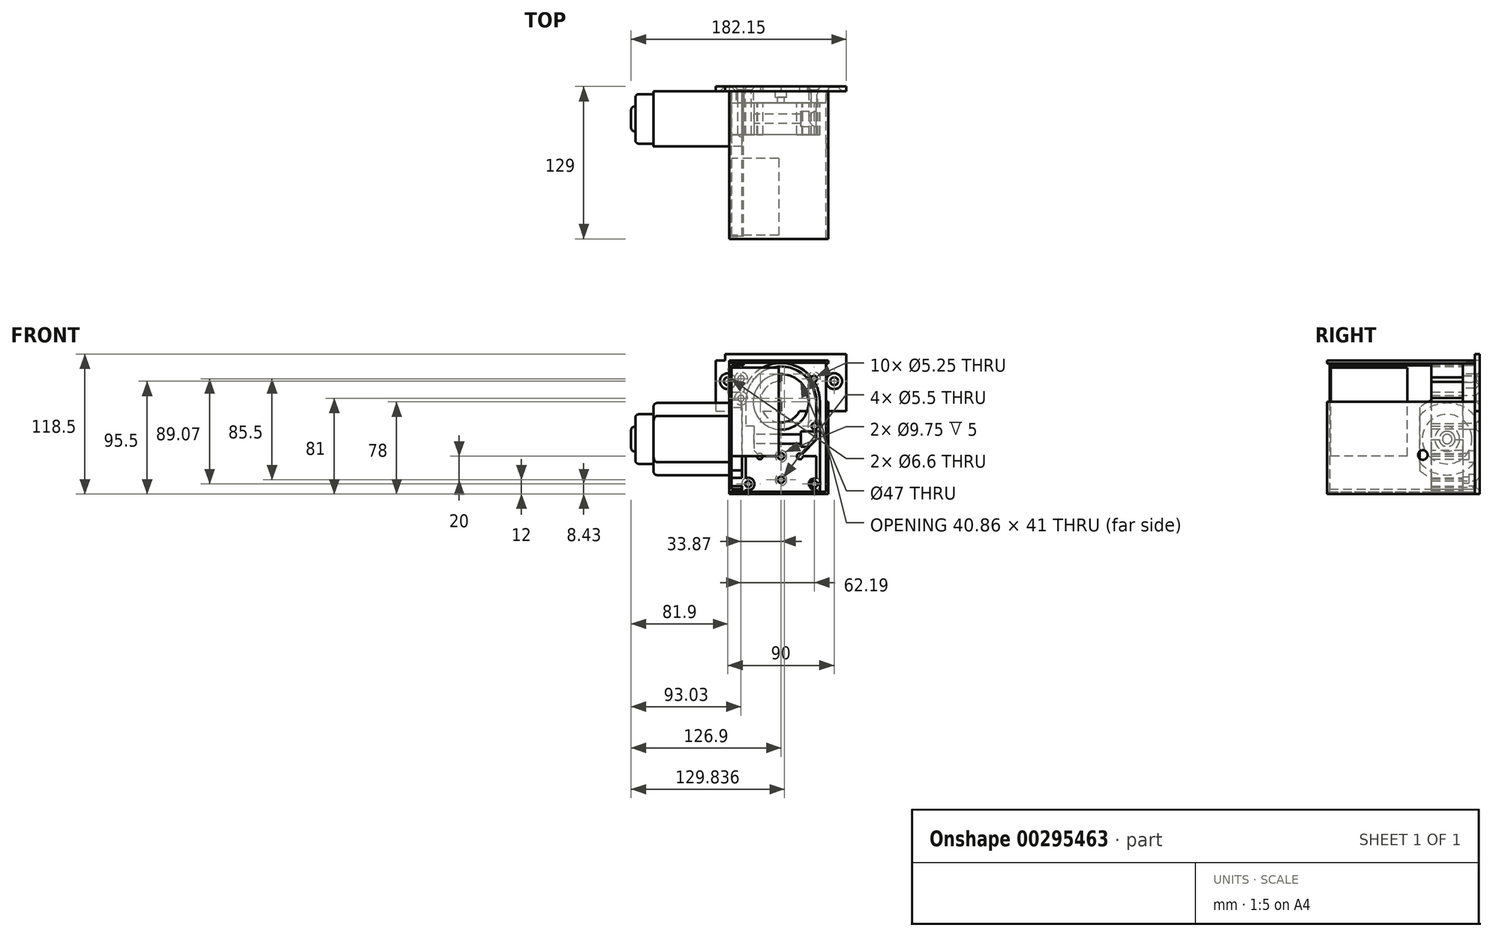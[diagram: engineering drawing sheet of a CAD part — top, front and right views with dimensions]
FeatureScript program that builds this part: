
annotation { "Feature Type Name" : "Feature", "Feature Type Description" : "" }
export const myFeature = defineFeature(function(context is Context, id is Id, definition is map)
    precondition{}
    {
        {
            var Q0;
            Q0=qCreatedBy(makeId("Front.planeOp"),FACE);
            cPlane(context, id + "F0", {"entities" : qUnion([Q0]), "cplaneType" : CPlaneType.OFFSET, "offset" : 4 * mm, "width" : 150 * mm, "height" : 150 * mm});
        }
        {
            var Q0;
            Q0=qCreatedBy(makeId("Front.planeOp"),FACE);
            cPlane(context, id + "F1", {"entities" : qUnion([Q0]), "cplaneType" : CPlaneType.OFFSET, "offset" : 14 * mm, "width" : 150 * mm, "height" : 150 * mm});
        }
        {
            var Q0;
            Q0=qCreatedBy(id+"F1.planeOp",FACE);
            var sketch = newSketch(context, id + "F2", { "sketchPlane" : qUnion([Q0])});
            skLineSegment(sketch, "E0", {"start": v(-56.01, 0) * mm, "end": v(61.33, 0) * mm, "construction": true});
            skLineSegment(sketch, "E1", {"start": v(0, 42.96) * mm, "end": v(0, -44.48) * mm, "construction": true});
            skLineSegment(sketch, "E2", {"start": v(55.25, 0) * mm, "end": v(55.25, 35) * mm});
            skLineSegment(sketch, "E3", {"start": v(55.25, 35) * mm, "end": v(0, 35) * mm});
            skLineSegment(sketch, "E4", {"start": v(0, 35) * mm, "end": v(-55.25, 35) * mm});
            skLineSegment(sketch, "E5", {"start": v(-55.25, 35) * mm, "end": v(-55.25, -35) * mm});
            skLineSegment(sketch, "E6", {"start": v(-55.25, -35) * mm, "end": v(55.25, -35) * mm});
            skLineSegment(sketch, "E7", {"start": v(55.25, -35) * mm, "end": v(55.25, 0) * mm});
            skLineSegment(sketch, "E8", {"start": v(-45, 0) * mm, "end": v(-45, 17.5) * mm, "construction": true});
            skLineSegment(sketch, "E9", {"start": v(-45, 17.5) * mm, "end": v(0, 17.5) * mm, "construction": true});
            skPoint(sketch, "E10", {"position": v(-45, 17.5) * mm});
            skPoint(sketch, "E11.MirrorP", {"position": v(45, 17.5) * mm});
            skCircle(sketch, "E12", {"center": v(0, 0) * mm, "radius": 23.5 * mm});
            skLineSegment(sketch, "E13.0", {"start": v(-53.25, 33) * mm, "end": v(-53.25, -35) * mm});
            skLineSegment(sketch, "E13.1", {"start": v(53.25, -35) * mm, "end": v(53.25, 0) * mm});
            skLineSegment(sketch, "E13.2", {"start": v(53.25, 0) * mm, "end": v(53.25, 33) * mm});
            skLineSegment(sketch, "E13.3", {"start": v(53.25, 33) * mm, "end": v(0, 33) * mm});
            skLineSegment(sketch, "E13.4", {"start": v(0, 33) * mm, "end": v(-53.25, 33) * mm});
            skCircle(sketch, "E14", {"center": v(0, 0) * mm, "radius": 32.9 * mm});
            skPoint(sketch, "E15", {"position": v(-32.9, 0) * mm});
            skLineSegment(sketch, "E16", {"start": v(-32.9, 0) * mm, "end": v(-32.9, -35) * mm});
            skLineSegment(sketch, "E17", {"start": v(-32.9, 0) * mm, "end": v(-55.25, 0) * mm});
            skLineSegment(sketch, "E18", {"start": v(-32.9, 0) * mm, "end": v(-32.9, 33) * mm});
            skLineSegment(sketch, "E19", {"start": v(-32.9, -35) * mm, "end": v(-32.9, -76) * mm});
            skLineSegment(sketch, "E20", {"start": v(-32.9, -76) * mm, "end": v(32.9, -76) * mm});
            skLineSegment(sketch, "E21", {"start": v(32.9, -76) * mm, "end": v(32.9, 33) * mm});
            skLineSegment(sketch, "E22", {"start": v(-41.9, 33) * mm, "end": v(-41.9, -76) * mm});
            skLineSegment(sketch, "E23", {"start": v(-41.9, -76) * mm, "end": v(-32.9, -76) * mm});
            skLineSegment(sketch, "E24", {"start": v(38.1, -76) * mm, "end": v(32.9, -76) * mm});
            skLineSegment(sketch, "E25", {"start": v(38.1, -76) * mm, "end": v(38.1, 33) * mm});
            skCircle(sketch, "E26", {"center": v(-45, 17.5) * mm, "radius": 6.75 * mm});
            skSolve(sketch);
        }
        {
            var Q0;
            Q0=qCreatedBy(id+"F0.planeOp",FACE);
            var sketch = newSketch(context, id + "F3", { "sketchPlane" : qUnion([Q0])});
            skCircle(sketch, "E27.0", {"center": v(0, 0) * mm, "radius": 23.5 * mm});
            skCircle(sketch, "E28.0", {"center": v(0, 0) * mm, "radius": 32.9 * mm, "construction": true});
            skLineSegment(sketch, "E29.0", {"start": v(53.25, 33) * mm, "end": v(0, 33) * mm});
            skLineSegment(sketch, "E29.1", {"start": v(0, 33) * mm, "end": v(-53.25, 33) * mm});
            skLineSegment(sketch, "E29.2", {"start": v(-53.25, 33) * mm, "end": v(-53.25, -35) * mm});
            skLineSegment(sketch, "E29.3", {"start": v(53.25, 0) * mm, "end": v(53.25, 33) * mm});
            skLineSegment(sketch, "E29.4", {"start": v(53.25, -35) * mm, "end": v(53.25, 0) * mm});
            skLineSegment(sketch, "E29.5", {"start": v(55.25, -35) * mm, "end": v(55.25, 0) * mm});
            skLineSegment(sketch, "E29.6", {"start": v(55.25, 0) * mm, "end": v(55.25, 35) * mm});
            skLineSegment(sketch, "E29.7", {"start": v(55.25, 35) * mm, "end": v(0, 35) * mm});
            skLineSegment(sketch, "E29.8", {"start": v(0, 35) * mm, "end": v(-55.25, 35) * mm});
            skLineSegment(sketch, "E29.9", {"start": v(-55.25, 35) * mm, "end": v(-55.25, -35) * mm});
            skPoint(sketch, "E29.10", {"position": v(-45, 17.5) * mm});
            skPoint(sketch, "E29.11", {"position": v(45, 17.5) * mm});
            skLineSegment(sketch, "E29.12", {"start": v(-45, 17.5) * mm, "end": v(0, 17.5) * mm});
            skLineSegment(sketch, "E29.13", {"start": v(-45, 0) * mm, "end": v(-45, 17.5) * mm});
            skLineSegment(sketch, "E29.14", {"start": v(-56.01, 0) * mm, "end": v(61.33, 0) * mm});
            skLineSegment(sketch, "E29.15", {"start": v(0, 42.96) * mm, "end": v(0, -44.48) * mm});
            skLineSegment(sketch, "E29.18", {"start": v(-32.9, 0) * mm, "end": v(-32.9, -35) * mm, "construction": true});
            skLineSegment(sketch, "E30.0", {"start": v(-55.25, -35) * mm, "end": v(55.25, -35) * mm});
            skCircle(sketch, "E31", {"center": v(0, 0) * mm, "radius": 17.5 * mm});
            skLineSegment(sketch, "E32", {"start": v(-55.25, -8) * mm, "end": v(55.25, -8) * mm});
            skLineSegment(sketch, "E33", {"start": v(48.1, 35) * mm, "end": v(48.1, -8) * mm, "construction": true});
            skLineSegment(sketch, "E34.0", {"start": v(32.9, -76) * mm, "end": v(32.9, 33) * mm});
            skLineSegment(sketch, "E34.1", {"start": v(-32.9, -76) * mm, "end": v(32.9, -76) * mm});
            skLineSegment(sketch, "E34.2", {"start": v(-41.9, 33) * mm, "end": v(-41.9, -76) * mm});
            skLineSegment(sketch, "E34.3", {"start": v(-41.9, -76) * mm, "end": v(-32.9, -76) * mm});
            skLineSegment(sketch, "E35.0", {"start": v(38.1, -76) * mm, "end": v(38.1, 33) * mm});
            skLineSegment(sketch, "E35.1", {"start": v(38.1, -76) * mm, "end": v(32.9, -76) * mm});
            skLineSegment(sketch, "E36.0", {"start": v(40.1, -76) * mm, "end": v(40.1, -8) * mm});
            skLineSegment(sketch, "E37", {"start": v(38.1, -76) * mm, "end": v(40.1, -76) * mm});
            skLineSegment(sketch, "E38", {"start": v(-43.9, -35) * mm, "end": v(-43.9, -76) * mm});
            skLineSegment(sketch, "E39", {"start": v(-43.9, -76) * mm, "end": v(-41.9, -76) * mm});
            skLineSegment(sketch, "E40", {"start": v(-43.9, -76) * mm, "end": v(-43.9, -78) * mm});
            skLineSegment(sketch, "E41", {"start": v(-43.9, -78) * mm, "end": v(40.1, -78) * mm});
            skLineSegment(sketch, "E42", {"start": v(40.1, -78) * mm, "end": v(40.1, -76) * mm});
            skLineSegment(sketch, "E43", {"start": v(-43.9, -35) * mm, "end": v(-43.9, -8) * mm});
            skLineSegment(sketch, "E44", {"start": v(-55.25, 35) * mm, "end": v(-55.25, 40.5) * mm});
            skLineSegment(sketch, "E45", {"start": v(-55.25, 40.5) * mm, "end": v(55.25, 40.5) * mm});
            skLineSegment(sketch, "E46", {"start": v(55.25, 40.5) * mm, "end": v(55.25, 35) * mm});
            skLineSegment(sketch, "E47.bottom", {"start": v(-55.25, 40.5) * mm, "end": v(-47.25, 40.5) * mm});
            skLineSegment(sketch, "E47.top", {"start": v(-55.25, 32.5) * mm, "end": v(-47.25, 32.5) * mm});
            skLineSegment(sketch, "E47.left", {"start": v(-55.25, 40.5) * mm, "end": v(-55.25, 32.5) * mm});
            skLineSegment(sketch, "E47.right", {"start": v(-47.25, 40.5) * mm, "end": v(-47.25, 32.5) * mm});
            skLineSegment(sketch, "E48.bottom", {"start": v(-47.25, 32.5) * mm, "end": v(47.25, 32.5) * mm});
            skLineSegment(sketch, "E48.top", {"start": v(-47.25, 0.5) * mm, "end": v(47.25, 0.5) * mm});
            skLineSegment(sketch, "E48.left", {"start": v(-47.25, 32.5) * mm, "end": v(-47.25, 0.5) * mm});
            skLineSegment(sketch, "E48.right", {"start": v(47.25, 32.5) * mm, "end": v(47.25, 0.5) * mm});
            skSolve(sketch);
        }
        {
            var Q0;
            {var subQ5=sQuery(id+"F3.wireOp",EDGE,"E48.left");Q0=makeQuery(id+"F3.imprint","IMPRINT",FACE,{"disambiguationData":[TD([[makeQuery(id+"F3.imprint","IMPRINT",EDGE,{"derivedFrom":subQ5}),-1.0]])]});}
            var Q1;
            {var subQ0=sQuery(id+"F3.wireOp",EDGE,"E32");var subQ1=makeQuery(id+"F3.imprint","INTERSECT",VERTEX,{"derivedFrom":[subQ0,sQuery(id+"F3.wireOp",EDGE,"E36.0")]});Q1=makeQuery(id+"F3.imprint","IMPRINT",FACE,{"disambiguationData":[TD([[makeQuery(id+"F3.imprint","IMPRINT",EDGE,{"disambiguationData":[TD([[subQ1,1.0]])],"derivedFrom":subQ0}),1.0]])]});}
            var Q2;
            {var subQ0=sQuery(id+"F3.wireOp",EDGE,"E29.13");var subQ1=sQuery(id+"F3.wireOp",EDGE,"E29.12");var subQ2=makeQuery(id+"F3.imprint","INTERSECT",VERTEX,{"derivedFrom":[subQ1,subQ0]});Q2=makeQuery(id+"F3.imprint","IMPRINT",FACE,{"disambiguationData":[TD([[makeQuery(id+"F3.imprint","IMPRINT",EDGE,{"disambiguationData":[TD([[subQ2,-1.0]])],"derivedFrom":subQ1}),-1.0]])]});}
            var Q3;
            {var subQ0=sQuery(id+"F3.wireOp",EDGE,"E29.14");var subQ1=sQuery(id+"F3.wireOp",EDGE,"E29.13");var subQ2=makeQuery(id+"F3.imprint","INTERSECT",VERTEX,{"derivedFrom":[subQ1,subQ0]});Q3=makeQuery(id+"F3.imprint","IMPRINT",FACE,{"disambiguationData":[TD([[makeQuery(id+"F3.imprint","IMPRINT",EDGE,{"disambiguationData":[TD([[subQ2,-1.0]])],"derivedFrom":subQ1}),-1.0]])]});}
            var Q4;
            {var subQ5=sQuery(id+"F3.wireOp",EDGE,"E29.3");Q4=makeQuery(id+"F3.imprint","IMPRINT",FACE,{"disambiguationData":[TD([[makeQuery(id+"F3.imprint","IMPRINT",EDGE,{"derivedFrom":subQ5}),1.0]])]});}
            var Q5;
            {var subQ5=sQuery(id+"F3.wireOp",EDGE,"E29.3");Q5=makeQuery(id+"F3.imprint","IMPRINT",FACE,{"disambiguationData":[TD([[makeQuery(id+"F3.imprint","IMPRINT",EDGE,{"derivedFrom":subQ5}),-1.0]])]});}
            var Q6;
            {var subQ1=sQuery(id+"F3.wireOp",EDGE,"E29.12");var subQ5=sQuery(id+"F3.wireOp",EDGE,"E34.2");var subQ6=makeQuery(id+"F3.imprint","INTERSECT",VERTEX,{"derivedFrom":[subQ1,subQ5]});Q6=makeQuery(id+"F3.imprint","IMPRINT",FACE,{"disambiguationData":[TD([[makeQuery(id+"F3.imprint","IMPRINT",EDGE,{"disambiguationData":[TD([[subQ6,-1.0]])],"derivedFrom":subQ1}),1.0]])]});}
            var Q7;
            {var subQ3=sQuery(id+"F3.wireOp",EDGE,"E32");var subQ5=sQuery(id+"F3.wireOp",EDGE,"E29.5");var subQ7=makeQuery(id+"F3.imprint","INTERSECT",VERTEX,{"derivedFrom":[subQ5,subQ3]});Q7=makeQuery(id+"F3.imprint","IMPRINT",FACE,{"disambiguationData":[TD([[makeQuery(id+"F3.imprint","IMPRINT",EDGE,{"disambiguationData":[TD([[subQ7,1.0]])],"derivedFrom":subQ3}),1.0]])]});}
            var Q8;
            {var subQ1=sQuery(id+"F3.wireOp",EDGE,"E29.1");var subQ7=makeQuery(id+"F3.imprint","INTERSECT",VERTEX,{"derivedFrom":[subQ1,sQuery(id+"F3.wireOp",EDGE,"E34.2")]});Q8=makeQuery(id+"F3.imprint","IMPRINT",FACE,{"disambiguationData":[TD([[makeQuery(id+"F3.imprint","IMPRINT",EDGE,{"disambiguationData":[TD([[subQ7,-1.0]])],"derivedFrom":subQ1}),-1.0]])]});}
            var Q9;
            {var subQ0=sQuery(id+"F3.wireOp",EDGE,"E31");var subQ1=sQuery(id+"F3.wireOp",EDGE,"E29.14");var subQ2=makeQuery(id+"F3.imprint","INTERSECT",VERTEX,{"disambiguationData":[OD(1.0)],"derivedFrom":[subQ1,subQ0]});Q9=makeQuery(id+"F3.imprint","IMPRINT",FACE,{"disambiguationData":[TD([[makeQuery(id+"F3.imprint","IMPRINT",EDGE,{"disambiguationData":[TD([[subQ2,-1.0]])],"derivedFrom":subQ1}),1.0]])]});}
            var Q10;
            {var subQ1=sQuery(id+"F3.wireOp",EDGE,"E29.12");var subQ3=sQuery(id+"F3.wireOp",EDGE,"E27.0");var subQ4=makeQuery(id+"F3.imprint","INTERSECT",VERTEX,{"derivedFrom":[subQ1,subQ3]});Q10=makeQuery(id+"F3.imprint","IMPRINT",FACE,{"disambiguationData":[TD([[makeQuery(id+"F3.imprint","IMPRINT",EDGE,{"disambiguationData":[TD([[subQ4,1.0]])],"derivedFrom":subQ3}),1.0]])]});}
            var Q11;
            {var subQ1=sQuery(id+"F3.wireOp",EDGE,"E29.12");var subQ3=sQuery(id+"F3.wireOp",EDGE,"E27.0");var subQ4=makeQuery(id+"F3.imprint","INTERSECT",VERTEX,{"derivedFrom":[subQ1,subQ3]});Q11=makeQuery(id+"F3.imprint","IMPRINT",FACE,{"disambiguationData":[TD([[makeQuery(id+"F3.imprint","IMPRINT",EDGE,{"disambiguationData":[TD([[subQ4,-1.0]])],"derivedFrom":subQ3}),1.0]])]});}
            var Q12;
            {var subQ0=sQuery(id+"F3.wireOp",EDGE,"E27.0");var subQ1=sQuery(id+"F3.wireOp",EDGE,"E29.14");var subQ2=makeQuery(id+"F3.imprint","INTERSECT",VERTEX,{"disambiguationData":[OD(0.0)],"derivedFrom":[subQ1,subQ0]});Q12=makeQuery(id+"F3.imprint","IMPRINT",FACE,{"disambiguationData":[TD([[makeQuery(id+"F3.imprint","IMPRINT",EDGE,{"disambiguationData":[TD([[subQ2,-1.0]])],"derivedFrom":subQ1}),-1.0]])]});}
            var Q13;
            {var subQ0=sQuery(id+"F3.wireOp",EDGE,"E31");var subQ1=sQuery(id+"F3.wireOp",EDGE,"E29.14");var subQ2=makeQuery(id+"F3.imprint","INTERSECT",VERTEX,{"disambiguationData":[OD(1.0)],"derivedFrom":[subQ1,subQ0]});Q13=makeQuery(id+"F3.imprint","IMPRINT",FACE,{"disambiguationData":[TD([[makeQuery(id+"F3.imprint","IMPRINT",EDGE,{"disambiguationData":[TD([[subQ2,-1.0]])],"derivedFrom":subQ1}),-1.0]])]});}
            var Q14;
            {var subQ0=sQuery(id+"F3.wireOp",EDGE,"E30.0");var subQ1=sQuery(id+"F3.wireOp",EDGE,"E29.15");var subQ2=makeQuery(id+"F3.imprint","INTERSECT",VERTEX,{"derivedFrom":[subQ1,subQ0]});Q14=makeQuery(id+"F3.imprint","IMPRINT",FACE,{"disambiguationData":[TD([[makeQuery(id+"F3.imprint","IMPRINT",EDGE,{"disambiguationData":[TD([[subQ2,1.0]])],"derivedFrom":subQ1}),1.0]])]});}
            var Q15;
            {var subQ0=sQuery(id+"F3.wireOp",EDGE,"E30.0");var subQ1=sQuery(id+"F3.wireOp",EDGE,"E29.15");var subQ2=makeQuery(id+"F3.imprint","INTERSECT",VERTEX,{"derivedFrom":[subQ1,subQ0]});Q15=makeQuery(id+"F3.imprint","IMPRINT",FACE,{"disambiguationData":[TD([[makeQuery(id+"F3.imprint","IMPRINT",EDGE,{"disambiguationData":[TD([[subQ2,1.0]])],"derivedFrom":subQ1}),-1.0]])]});}
            var Q16;
            {var subQ0=sQuery(id+"F3.wireOp",EDGE,"E31");var subQ1=sQuery(id+"F3.wireOp",EDGE,"E29.15");var subQ2=makeQuery(id+"F3.imprint","INTERSECT",VERTEX,{"derivedFrom":[subQ1,subQ0]});Q16=makeQuery(id+"F3.imprint","IMPRINT",FACE,{"disambiguationData":[TD([[makeQuery(id+"F3.imprint","IMPRINT",EDGE,{"disambiguationData":[TD([[subQ2,-1.0]])],"derivedFrom":subQ1}),-1.0]])]});}
            var Q17;
            {var subQ0=sQuery(id+"F3.wireOp",EDGE,"E31");var subQ1=sQuery(id+"F3.wireOp",EDGE,"E29.15");var subQ2=makeQuery(id+"F3.imprint","INTERSECT",VERTEX,{"derivedFrom":[subQ1,subQ0]});Q17=makeQuery(id+"F3.imprint","IMPRINT",FACE,{"disambiguationData":[TD([[makeQuery(id+"F3.imprint","IMPRINT",EDGE,{"disambiguationData":[TD([[subQ2,-1.0]])],"derivedFrom":subQ1}),1.0]])]});}
            var Q18;
            {var subQ0=sQuery(id+"F3.wireOp",EDGE,"E27.0");var subQ1=sQuery(id+"F3.wireOp",EDGE,"E29.14");var subQ2=makeQuery(id+"F3.imprint","INTERSECT",VERTEX,{"disambiguationData":[OD(1.0)],"derivedFrom":[subQ1,subQ0]});Q18=makeQuery(id+"F3.imprint","IMPRINT",FACE,{"disambiguationData":[TD([[makeQuery(id+"F3.imprint","IMPRINT",EDGE,{"disambiguationData":[TD([[subQ2,-1.0]])],"derivedFrom":subQ1}),-1.0]])]});}
            var Q19;
            {var subQ0=sQuery(id+"F3.wireOp",EDGE,"E34.2");var subQ1=sQuery(id+"F3.wireOp",EDGE,"E29.14");var subQ2=makeQuery(id+"F3.imprint","INTERSECT",VERTEX,{"derivedFrom":[subQ1,subQ0]});Q19=makeQuery(id+"F3.imprint","IMPRINT",FACE,{"disambiguationData":[TD([[makeQuery(id+"F3.imprint","IMPRINT",EDGE,{"disambiguationData":[TD([[subQ2,-1.0]])],"derivedFrom":subQ1}),-1.0]])]});}
            var Q20;
            {var subQ0=sQuery(id+"F3.wireOp",EDGE,"E34.2");var subQ1=sQuery(id+"F3.wireOp",EDGE,"E29.12");var subQ2=makeQuery(id+"F3.imprint","INTERSECT",VERTEX,{"derivedFrom":[subQ1,subQ0]});Q20=makeQuery(id+"F3.imprint","IMPRINT",FACE,{"disambiguationData":[TD([[makeQuery(id+"F3.imprint","IMPRINT",EDGE,{"disambiguationData":[TD([[subQ2,-1.0]])],"derivedFrom":subQ1}),-1.0]])]});}
            var Q21;
            {var subQ2=sQuery(id+"F3.wireOp",EDGE,"E29.2");var subQ4=sQuery(id+"F3.wireOp",EDGE,"E29.14");var subQ8=makeQuery(id+"F3.imprint","INTERSECT",VERTEX,{"derivedFrom":[subQ2,subQ4]});Q21=makeQuery(id+"F3.imprint","IMPRINT",FACE,{"disambiguationData":[TD([[makeQuery(id+"F3.imprint","IMPRINT",EDGE,{"disambiguationData":[TD([[subQ8,-1.0]])],"derivedFrom":subQ2}),1.0]])]});}
            var Q22;
            {var subQ0=sQuery(id+"F3.wireOp",EDGE,"E29.14");var subQ1=sQuery(id+"F3.wireOp",EDGE,"E29.2");var subQ2=makeQuery(id+"F3.imprint","INTERSECT",VERTEX,{"derivedFrom":[subQ1,subQ0]});Q22=makeQuery(id+"F3.imprint","IMPRINT",FACE,{"disambiguationData":[TD([[makeQuery(id+"F3.imprint","IMPRINT",EDGE,{"disambiguationData":[TD([[subQ2,-1.0]])],"derivedFrom":subQ1}),-1.0]])]});}
            var Q23;
            {var subQ0=sQuery(id+"F3.wireOp",EDGE,"E34.1");Q23=makeQuery(id+"F3.imprint","IMPRINT",FACE,{"disambiguationData":[TD([[makeQuery(id+"F3.imprint","IMPRINT",EDGE,{"derivedFrom":subQ0}),1.0]])]});}
            var Q24;
            {var subQ0=sQuery(id+"F3.wireOp",EDGE,"E27.0");var subQ1=sQuery(id+"F3.wireOp",EDGE,"E29.14");var subQ2=makeQuery(id+"F3.imprint","INTERSECT",VERTEX,{"disambiguationData":[OD(1.0)],"derivedFrom":[subQ1,subQ0]});Q24=makeQuery(id+"F3.imprint","IMPRINT",FACE,{"disambiguationData":[TD([[makeQuery(id+"F3.imprint","IMPRINT",EDGE,{"disambiguationData":[TD([[subQ2,-1.0]])],"derivedFrom":subQ1}),1.0]])]});}
            var Q25;
            {var subQ5=sQuery(id+"F3.wireOp",EDGE,"E35.1");Q25=makeQuery(id+"F3.imprint","IMPRINT",FACE,{"disambiguationData":[TD([[makeQuery(id+"F3.imprint","IMPRINT",EDGE,{"derivedFrom":subQ5}),-1.0]])]});}
            var Q26;
            {var subQ0=sQuery(id+"F3.wireOp",EDGE,"E34.0");var subQ1=sQuery(id+"F3.wireOp",EDGE,"E30.0");var subQ2=makeQuery(id+"F3.imprint","INTERSECT",VERTEX,{"derivedFrom":[subQ1,subQ0]});Q26=makeQuery(id+"F3.imprint","IMPRINT",FACE,{"disambiguationData":[TD([[makeQuery(id+"F3.imprint","IMPRINT",EDGE,{"disambiguationData":[TD([[subQ2,-1.0]])],"derivedFrom":subQ1}),1.0]])]});}
            var Q27;
            {var subQ0=sQuery(id+"F3.wireOp",EDGE,"E34.0");var subQ1=sQuery(id+"F3.wireOp",EDGE,"E29.14");var subQ2=makeQuery(id+"F3.imprint","INTERSECT",VERTEX,{"derivedFrom":[subQ1,subQ0]});Q27=makeQuery(id+"F3.imprint","IMPRINT",FACE,{"disambiguationData":[TD([[makeQuery(id+"F3.imprint","IMPRINT",EDGE,{"disambiguationData":[TD([[subQ2,-1.0]])],"derivedFrom":subQ1}),-1.0]])]});}
            var Q28;
            {var subQ0=sQuery(id+"F3.wireOp",EDGE,"E34.0");var subQ1=sQuery(id+"F3.wireOp",EDGE,"E29.0");var subQ2=makeQuery(id+"F3.imprint","INTERSECT",VERTEX,{"derivedFrom":[subQ1,subQ0]});Q28=makeQuery(id+"F3.imprint","IMPRINT",FACE,{"disambiguationData":[TD([[makeQuery(id+"F3.imprint","IMPRINT",EDGE,{"disambiguationData":[TD([[subQ2,1.0]])],"derivedFrom":subQ1}),1.0]])]});}
            var Q29;
            {var subQ5=sQuery(id+"F3.wireOp",EDGE,"E37");Q29=makeQuery(id+"F3.imprint","IMPRINT",FACE,{"disambiguationData":[TD([[makeQuery(id+"F3.imprint","IMPRINT",EDGE,{"derivedFrom":subQ5}),1.0]])]});}
            var Q30;
            {var subQ0=sQuery(id+"F3.wireOp",EDGE,"E36.0");var subQ1=sQuery(id+"F3.wireOp",EDGE,"E30.0");var subQ2=makeQuery(id+"F3.imprint","INTERSECT",VERTEX,{"derivedFrom":[subQ1,subQ0]});Q30=makeQuery(id+"F3.imprint","IMPRINT",FACE,{"disambiguationData":[TD([[makeQuery(id+"F3.imprint","IMPRINT",EDGE,{"disambiguationData":[TD([[subQ2,1.0]])],"derivedFrom":subQ1}),1.0]])]});}
            var Q31;
            {var subQ0=sQuery(id+"F3.wireOp",EDGE,"E38");Q31=makeQuery(id+"F3.imprint","IMPRINT",FACE,{"disambiguationData":[TD([[makeQuery(id+"F3.imprint","IMPRINT",EDGE,{"derivedFrom":subQ0}),1.0]])]});}
            var Q32;
            Q32=makeQuery(id+"F3.imprint","IMPRINT",FACE,{"disambiguationData":[TD([[makeQuery(id+"F3.imprint","IMPRINT",EDGE,{"derivedFrom":sQuery(id+"F3.wireOp",EDGE,"E34.1")}),-1.0]])]});
            var Q33;
            {var subQ0=sQuery(id+"F3.wireOp",EDGE,"E43");Q33=makeQuery(id+"F3.imprint","IMPRINT",FACE,{"disambiguationData":[TD([[makeQuery(id+"F3.imprint","IMPRINT",EDGE,{"derivedFrom":subQ0}),-1.0]])]});}
            var Q34;
            {var subQ5=sQuery(id+"F3.wireOp",EDGE,"E47.bottom");Q34=makeQuery(id+"F3.imprint","IMPRINT",FACE,{"disambiguationData":[TD([[makeQuery(id+"F3.imprint","IMPRINT",EDGE,{"derivedFrom":subQ5}),-1.0]])]});}
            var Q35;
            {var subQ1=sQuery(id+"F3.wireOp",EDGE,"E29.8");var subQ3=sQuery(id+"F3.wireOp",EDGE,"E47.right");var subQ4=makeQuery(id+"F3.imprint","INTERSECT",VERTEX,{"derivedFrom":[subQ1,subQ3]});Q35=makeQuery(id+"F3.imprint","IMPRINT",FACE,{"disambiguationData":[TD([[makeQuery(id+"F3.imprint","IMPRINT",EDGE,{"disambiguationData":[TD([[subQ4,1.0]])],"derivedFrom":subQ1}),-1.0]])]});}
            var Q36;
            {var subQ0=sQuery(id+"F3.wireOp",EDGE,"E29.7");Q36=makeQuery(id+"F3.imprint","IMPRINT",FACE,{"disambiguationData":[TD([[makeQuery(id+"F3.imprint","IMPRINT",EDGE,{"derivedFrom":subQ0}),-1.0]])]});}
            var Q37;
            {var subQ3=sQuery(id+"F3.wireOp",EDGE,"E29.2");var subQ9=sQuery(id+"F3.wireOp",EDGE,"E29.1");var subQ10=makeQuery(id+"F3.imprint","INTERSECT",VERTEX,{"derivedFrom":[subQ9,subQ3]});Q37=makeQuery(id+"F3.imprint","IMPRINT",FACE,{"disambiguationData":[TD([[makeQuery(id+"F3.imprint","IMPRINT",EDGE,{"disambiguationData":[TD([[subQ10,1.0]])],"derivedFrom":subQ9}),-1.0]])]});}
            var Q38;
            {var subQ0=sQuery(id+"F3.wireOp",EDGE,"E47.top");var subQ1=sQuery(id+"F3.wireOp",EDGE,"E29.2");var subQ2=makeQuery(id+"F3.imprint","INTERSECT",VERTEX,{"derivedFrom":[subQ1,subQ0]});Q38=makeQuery(id+"F3.imprint","IMPRINT",FACE,{"disambiguationData":[TD([[makeQuery(id+"F3.imprint","IMPRINT",EDGE,{"disambiguationData":[TD([[subQ2,-1.0]])],"derivedFrom":subQ1}),-1.0]])]});}
            var Q39;
            {var subQ0=sQuery(id+"F3.wireOp",EDGE,"E48.bottom");var subQ1=sQuery(id+"F3.wireOp",EDGE,"E29.15");var subQ2=makeQuery(id+"F3.imprint","INTERSECT",VERTEX,{"derivedFrom":[subQ1,subQ0]});Q39=makeQuery(id+"F3.imprint","IMPRINT",FACE,{"disambiguationData":[TD([[makeQuery(id+"F3.imprint","IMPRINT",EDGE,{"disambiguationData":[TD([[subQ2,-1.0]])],"derivedFrom":subQ1}),1.0]])]});}
            var Q40;
            {var subQ5=sQuery(id+"F3.wireOp",EDGE,"E48.right");Q40=makeQuery(id+"F3.imprint","IMPRINT",FACE,{"disambiguationData":[TD([[makeQuery(id+"F3.imprint","IMPRINT",EDGE,{"derivedFrom":subQ5}),-1.0]])]});}
            var Q41;
            {var subQ0=sQuery(id+"F3.wireOp",EDGE,"E48.top");var subQ1=sQuery(id+"F3.wireOp",EDGE,"E34.0");var subQ2=makeQuery(id+"F3.imprint","INTERSECT",VERTEX,{"derivedFrom":[subQ1,subQ0]});Q41=makeQuery(id+"F3.imprint","IMPRINT",FACE,{"disambiguationData":[TD([[makeQuery(id+"F3.imprint","IMPRINT",EDGE,{"disambiguationData":[TD([[subQ2,-1.0]])],"derivedFrom":subQ1}),-1.0]])]});}
            var Q42;
            {var subQ1=sQuery(id+"F3.wireOp",EDGE,"E29.15");var subQ3=sQuery(id+"F3.wireOp",EDGE,"E27.0");var subQ4=makeQuery(id+"F3.imprint","INTERSECT",VERTEX,{"disambiguationData":[OD(0.0)],"derivedFrom":[subQ1,subQ3]});Q42=makeQuery(id+"F3.imprint","IMPRINT",FACE,{"disambiguationData":[TD([[makeQuery(id+"F3.imprint","IMPRINT",EDGE,{"disambiguationData":[TD([[subQ4,1.0]])],"derivedFrom":subQ3}),1.0]])]});}
            var Q43;
            {var subQ0=sQuery(id+"F3.wireOp",EDGE,"E34.0");var subQ1=sQuery(id+"F3.wireOp",EDGE,"E29.14");var subQ2=makeQuery(id+"F3.imprint","INTERSECT",VERTEX,{"derivedFrom":[subQ1,subQ0]});Q43=makeQuery(id+"F3.imprint","IMPRINT",FACE,{"disambiguationData":[TD([[makeQuery(id+"F3.imprint","IMPRINT",EDGE,{"disambiguationData":[TD([[subQ2,-1.0]])],"derivedFrom":subQ1}),1.0]])]});}
            var Q44;
            {var subQ0=sQuery(id+"F3.wireOp",EDGE,"E34.2");var subQ1=sQuery(id+"F3.wireOp",EDGE,"E29.14");var subQ2=makeQuery(id+"F3.imprint","INTERSECT",VERTEX,{"derivedFrom":[subQ1,subQ0]});Q44=makeQuery(id+"F3.imprint","IMPRINT",FACE,{"disambiguationData":[TD([[makeQuery(id+"F3.imprint","IMPRINT",EDGE,{"disambiguationData":[TD([[subQ2,-1.0]])],"derivedFrom":subQ1}),1.0]])]});}
            var Q45;
            {var subQ0=sQuery(id+"F3.wireOp",EDGE,"E27.0");var subQ1=sQuery(id+"F3.wireOp",EDGE,"E29.14");var subQ2=makeQuery(id+"F3.imprint","INTERSECT",VERTEX,{"disambiguationData":[OD(0.0)],"derivedFrom":[subQ1,subQ0]});Q45=makeQuery(id+"F3.imprint","IMPRINT",FACE,{"disambiguationData":[TD([[makeQuery(id+"F3.imprint","IMPRINT",EDGE,{"disambiguationData":[TD([[subQ2,-1.0]])],"derivedFrom":subQ1}),1.0]])]});}
            var Q46;
            {var subQ1=sQuery(id+"F3.wireOp",EDGE,"E29.0");var subQ3=sQuery(id+"F3.wireOp",EDGE,"E34.0");var subQ4=makeQuery(id+"F3.imprint","INTERSECT",VERTEX,{"derivedFrom":[subQ1,subQ3]});Q46=makeQuery(id+"F3.imprint","IMPRINT",FACE,{"disambiguationData":[TD([[makeQuery(id+"F3.imprint","IMPRINT",EDGE,{"disambiguationData":[TD([[subQ4,1.0]])],"derivedFrom":subQ3}),1.0]])]});}
            var Q47;
            {var subQ1=sQuery(id+"F3.wireOp",EDGE,"E29.1");var subQ3=sQuery(id+"F3.wireOp",EDGE,"E34.2");var subQ4=makeQuery(id+"F3.imprint","INTERSECT",VERTEX,{"derivedFrom":[subQ1,subQ3]});Q47=makeQuery(id+"F3.imprint","IMPRINT",FACE,{"disambiguationData":[TD([[makeQuery(id+"F3.imprint","IMPRINT",EDGE,{"disambiguationData":[TD([[subQ4,-1.0]])],"derivedFrom":subQ3}),1.0]])]});}
            var Q48;
            {var subQ0=sQuery(id+"F3.wireOp",EDGE,"E48.left");Q48=makeQuery(id+"F3.imprint","IMPRINT",FACE,{"disambiguationData":[TD([[makeQuery(id+"F3.imprint","IMPRINT",EDGE,{"derivedFrom":subQ0}),1.0]])]});}
            var Q49;
            {var subQ0=sQuery(id+"F3.wireOp",EDGE,"E34.2");var subQ1=sQuery(id+"F3.wireOp",EDGE,"E29.1");var subQ2=makeQuery(id+"F3.imprint","INTERSECT",VERTEX,{"derivedFrom":[subQ1,subQ0]});Q49=makeQuery(id+"F3.imprint","IMPRINT",FACE,{"disambiguationData":[TD([[makeQuery(id+"F3.imprint","IMPRINT",EDGE,{"disambiguationData":[TD([[subQ2,-1.0]])],"derivedFrom":subQ1}),1.0]])]});}
            var Q50;
            {var subQ0=sQuery(id+"F3.wireOp",EDGE,"E29.2");var subQ1=sQuery(id+"F3.wireOp",EDGE,"E29.1");var subQ2=makeQuery(id+"F3.imprint","INTERSECT",VERTEX,{"derivedFrom":[subQ1,subQ0]});Q50=makeQuery(id+"F3.imprint","IMPRINT",FACE,{"disambiguationData":[TD([[makeQuery(id+"F3.imprint","IMPRINT",EDGE,{"disambiguationData":[TD([[subQ2,1.0]])],"derivedFrom":subQ1}),1.0]])]});}
            extrude(context, id + "F4", {"entities" : qUnion([Q0, Q1, Q2, Q3, Q4, Q5, Q6, Q7, Q8, Q9, Q10, Q11, Q12, Q13, Q14, Q15, Q16, Q17, Q18, Q19, Q20, Q21, Q22, Q23, Q24, Q25, Q26, Q27, Q28, Q29, Q30, Q31, Q32, Q33, Q34, Q35, Q36, Q37, Q38, Q39, Q40, Q41, Q42, Q43, Q44, Q45, Q46, Q47, Q48, Q49, Q50]), "oppositeDirection" : true, "depth" : 4 * mm});
        }
        {
            var Q0;
            {var subQ0=sQuery(id+"F2.wireOp",EDGE,"E16");Q0=makeQuery(id+"F2.imprint","IMPRINT",FACE,{"disambiguationData":[TD([[makeQuery(id+"F2.imprint","IMPRINT",EDGE,{"derivedFrom":subQ0}),1.0]])]});}
            var Q1;
            {var subQ0=sQuery(id+"F2.wireOp",EDGE,"E16");Q1=makeQuery(id+"F2.imprint","IMPRINT",FACE,{"disambiguationData":[TD([[makeQuery(id+"F2.imprint","IMPRINT",EDGE,{"derivedFrom":subQ0}),-1.0]])]});}
            var Q2;
            {var subQ0=sQuery(id+"F2.wireOp",EDGE,"E18");Q2=makeQuery(id+"F2.imprint","IMPRINT",FACE,{"disambiguationData":[TD([[makeQuery(id+"F2.imprint","IMPRINT",EDGE,{"derivedFrom":subQ0}),1.0]])]});}
            var Q3;
            {var subQ0=sQuery(id+"F2.wireOp",EDGE,"E18");Q3=makeQuery(id+"F2.imprint","IMPRINT",FACE,{"disambiguationData":[TD([[makeQuery(id+"F2.imprint","IMPRINT",EDGE,{"derivedFrom":subQ0}),-1.0]])]});}
            var Q4;
            Q4=makeQuery(id+"F2.imprint","IMPRINT",FACE,{"disambiguationData":[TD([[makeQuery(id+"F2.imprint","IMPRINT",EDGE,{"derivedFrom":sQuery(id+"F2.wireOp",EDGE,"E12")}),-1.0]])]});
            var Q5;
            {var subQ0=sQuery(id+"F2.wireOp",EDGE,"E19");Q5=makeQuery(id+"F2.imprint","IMPRINT",FACE,{"disambiguationData":[TD([[makeQuery(id+"F2.imprint","IMPRINT",EDGE,{"derivedFrom":subQ0}),1.0]])]});}
            var Q6;
            {var subQ0=sQuery(id+"F2.wireOp",EDGE,"E19");Q6=makeQuery(id+"F2.imprint","IMPRINT",FACE,{"disambiguationData":[TD([[makeQuery(id+"F2.imprint","IMPRINT",EDGE,{"derivedFrom":subQ0}),-1.0]])]});}
            var Q7;
            {var subQ0=sQuery(id+"F2.wireOp",EDGE,"E16");Q7=makeQuery(id+"F2.imprint","IMPRINT",FACE,{"disambiguationData":[TD([[makeQuery(id+"F2.imprint","IMPRINT",EDGE,{"derivedFrom":subQ0}),1.0]])]});}
            var Q8;
            {var subQ5=sQuery(id+"F2.wireOp",EDGE,"E24");Q8=makeQuery(id+"F2.imprint","IMPRINT",FACE,{"disambiguationData":[TD([[makeQuery(id+"F2.imprint","IMPRINT",EDGE,{"derivedFrom":subQ5}),-1.0]])]});}
            var Q9;
            {var subQ1=sQuery(id+"F2.wireOp",EDGE,"E6");var subQ6=sQuery(id+"F2.wireOp",EDGE,"E25");var subQ8=makeQuery(id+"F2.imprint","INTERSECT",VERTEX,{"derivedFrom":[subQ1,subQ6]});Q9=makeQuery(id+"F2.imprint","IMPRINT",FACE,{"disambiguationData":[TD([[makeQuery(id+"F2.imprint","IMPRINT",EDGE,{"disambiguationData":[TD([[subQ8,1.0]])],"derivedFrom":subQ1}),1.0]])]});}
            extrude(context, id + "F5", {"entities" : qUnion([Q0, Q1, Q2, Q3, Q4, Q5, Q6, Q7, Q8, Q9]), "oppositeDirection" : true, "depth" : 10 * mm});
        }
        {
            var Q0;
            Q0=sQuery(id+"F3.wireOp",VERTEX,"E29.10");
            var Q1;
            Q1=sQuery(id+"F3.wireOp",VERTEX,"E29.11");
            var Q2;
            Q2=makeQuery(id+"F4.opExtrude","SWEPT_BODY",BODY,{"disambiguationData":[OSD([sQuery(id+"F3.wireOp",EDGE,"E29.5"),sQuery(id+"F3.wireOp",EDGE,"E29.6"),sQuery(id+"F3.wireOp",EDGE,"E29.7"),sQuery(id+"F3.wireOp",EDGE,"E29.8"),sQuery(id+"F3.wireOp",EDGE,"E29.9"),sQuery(id+"F3.wireOp",EDGE,"E27.0"),sQuery(id+"F3.wireOp",EDGE,"E30.0")])]});
            hole(context, id + "F6", {"style" : HoleStyle.C_SINK, "endStyle" : HoleEndStyle.THROUGH, "holeDiameter" : 6.6 * mm, "cSinkDiameter" : 13.44 * mm, "cSinkAngle" : 90 * degree, "startFromSketch" : true, "locations" : qUnion([Q0, Q1]), "scope" : qUnion([Q2]), "isTappedThrough" : true});
        }
        {
            var Q0;
            Q0=qCreatedBy(id+"F1.planeOp",FACE);
            var sketch = newSketch(context, id + "F7", { "sketchPlane" : qUnion([Q0])});
            skArc(sketch, "E49", {"start": v(26.62, -19.34) * mm, "mid": v(27.7, -17.74) * mm, "end": v(28.7, -16.09) * mm});
            skLineSegment(sketch, "E50", {"start": v(0, 32.9) * mm, "end": v(0, -76.1) * mm, "construction": true});
            skLineSegment(sketch, "E51", {"start": v(32.9, 0) * mm, "end": v(32.9, -76.1) * mm});
            skLineSegment(sketch, "E52.MirrorCS", {"start": v(-32.9, 0) * mm, "end": v(-32.9, -76.1) * mm});
            skLineSegment(sketch, "E53", {"start": v(-32.9, -76.1) * mm, "end": v(32.9, -76.1) * mm});
            skLineSegment(sketch, "E54", {"start": v(0, 0) * mm, "end": v(-32.9, 0) * mm, "construction": true});
            skLineSegment(sketch, "E55", {"start": v(0, 0) * mm, "end": v(26.95, 18.87) * mm, "construction": true});
            skLineSegment(sketch, "E56", {"start": v(0, 0) * mm, "end": v(26.62, -19.34) * mm, "construction": true});
            skLineSegment(sketch, "E57", {"start": v(0, 0) * mm, "end": v(27.85, 19.5) * mm, "construction": true});
            skLineSegment(sketch, "E58", {"start": v(0, 0) * mm, "end": v(28.32, -20.57) * mm, "construction": true});
            skLineSegment(sketch, "E59", {"start": v(0, 0) * mm, "end": v(-34, 0) * mm, "construction": true});
            skCircle(sketch, "E60", {"center": v(0, 0) * mm, "radius": 34 * mm, "construction": true});
            skLineSegment(sketch, "E61", {"start": v(0, 0) * mm, "end": v(-33.87, 2.96) * mm, "construction": true});
            skPoint(sketch, "E62", {"position": v(-33.87, 2.96) * mm});
            skPoint(sketch, "E63", {"position": v(27.85, 19.5) * mm});
            skPoint(sketch, "E64", {"position": v(28.32, -20.57) * mm});
            skCircle(sketch, "E65", {"center": v(27.85, 19.5) * mm, "radius": 4.1 * mm});
            skCircle(sketch, "E66", {"center": v(28.32, -20.57) * mm, "radius": 4.5 * mm});
            skLineSegment(sketch, "E67", {"start": v(-41.9, -71.5) * mm, "end": v(-32.9, -71.5) * mm});
            skArc(sketch, "E68.trimOffspring", {"start": v(32.9, 0) * mm, "mid": v(0, 32.9) * mm, "end": v(-32.9, 0) * mm});
            skLineSegment(sketch, "E69.0", {"start": v(29.9, 0) * mm, "end": v(29.9, -76.1) * mm});
            skArc(sketch, "E69.1", {"start": v(29.9, 0) * mm, "mid": v(0, 29.9) * mm, "end": v(-29.9, 0) * mm});
            skLineSegment(sketch, "E69.2", {"start": v(-29.9, 0) * mm, "end": v(-29.9, -76.1) * mm});
            skLineSegment(sketch, "E70", {"start": v(28.32, -20.57) * mm, "end": v(28.32, -69.57) * mm, "construction": true});
            skLineSegment(sketch, "E71", {"start": v(28.32, -69.57) * mm, "end": v(-27.68, -69.57) * mm, "construction": true});
            skPoint(sketch, "E72", {"position": v(-27.68, -69.57) * mm});
            skPoint(sketch, "E73", {"position": v(28.32, -69.57) * mm});
            skCircle(sketch, "E74", {"center": v(-27.68, -69.57) * mm, "radius": 5.22 * mm});
            skCircle(sketch, "E75", {"center": v(28.32, -69.57) * mm, "radius": 4.58 * mm});
            skCircle(sketch, "E76", {"center": v(0, 0) * mm, "radius": 29.15 * mm});
            skLineSegment(sketch, "E77", {"start": v(32.9, 0) * mm, "end": v(31.95, 19.7) * mm});
            skLineSegment(sketch, "E78", {"start": v(12.8, 30.3) * mm, "end": v(29.45, 23.28) * mm});
            skLineSegment(sketch, "E79", {"start": v(-41.9, 8.5) * mm, "end": v(-31.78, 8.5) * mm});
            skLineSegment(sketch, "E80", {"start": v(-41.9, -71.5) * mm, "end": v(-41.9, 0) * mm});
            skLineSegment(sketch, "E81", {"start": v(-41.9, 0) * mm, "end": v(-32.9, 0) * mm});
            skLineSegment(sketch, "E82", {"start": v(-41.9, 0) * mm, "end": v(-41.9, 8.5) * mm});
            skPoint(sketch, "E83", {"position": v(15.9, -46.1) * mm});
            skCircle(sketch, "E84", {"center": v(15.9, -46.1) * mm, "radius": 2.5 * mm});
            skPoint(sketch, "E85", {"position": v(-17.9, -46.1) * mm});
            skLineSegment(sketch, "E86", {"start": v(15.9, -46.1) * mm, "end": v(-17.9, -46.1) * mm, "construction": true});
            skCircle(sketch, "E87", {"center": v(-17.9, -46.1) * mm, "radius": 2.5 * mm});
            skLineSegment(sketch, "E88", {"start": v(29.9, -46.1) * mm, "end": v(15.9, -46.1) * mm});
            skLineSegment(sketch, "E89", {"start": v(-17.9, -46.1) * mm, "end": v(-29.9, -46.1) * mm});
            skLineSegment(sketch, "E90", {"start": v(-17.9, -46.1) * mm, "end": v(-29.9, -34.1) * mm});
            skLineSegment(sketch, "E91", {"start": v(15.9, -46.1) * mm, "end": v(29.9, -32.1) * mm});
            skSolve(sketch);
        }
        {
            var Q0;
            {var subQ0=sQuery(id+"F7.wireOp",EDGE,"E68.trimOffspring");var subQ11=sQuery(id+"F7.wireOp",EDGE,"E52.MirrorCS");var subQ12=makeQuery(id+"F7.imprint","INTERSECT",VERTEX,{"derivedFrom":[subQ11,subQ0]});Q0=makeQuery(id+"F7.imprint","IMPRINT",FACE,{"disambiguationData":[TD([[makeQuery(id+"F7.imprint","IMPRINT",EDGE,{"disambiguationData":[TD([[subQ12,-1.0]])],"derivedFrom":subQ11}),1.0]])]});}
            var Q1;
            {var subQ0=sQuery(id+"F7.wireOp",EDGE,"OlHOJkcE-dCJ6-QTba-rwvD-c7LqSvl2V1iB");Q1=makeQuery(id+"F7.imprint","IMPRINT",FACE,{"disambiguationData":[TD([[makeQuery(id+"F7.imprint","IMPRINT",EDGE,{"derivedFrom":subQ0}),-1.0]])]});}
            var Q2;
            {var subQ0=sQuery(id+"F7.wireOp",EDGE,"E65");var subQ1=makeQuery(id+"F7.imprint","INTERSECT",VERTEX,{"derivedFrom":[subQ0,sQuery(id+"F7.wireOp",EDGE,"OlHOJkcE-dCJ6-QTba-rwvD-c7LqSvl2V1iB")]});Q2=makeQuery(id+"F7.imprint","IMPRINT",FACE,{"disambiguationData":[TD([[makeQuery(id+"F7.imprint","IMPRINT",EDGE,{"disambiguationData":[TD([[subQ1,1.0]])],"derivedFrom":subQ0}),1.0]])]});}
            var Q3;
            {var subQ0=sQuery(id+"F7.wireOp",EDGE,"E68.trimOffspring");var subQ1=sQuery(id+"F7.wireOp",EDGE,"E65");var subQ2=makeQuery(id+"F7.imprint","INTERSECT",VERTEX,{"disambiguationData":[OD(0.0)],"derivedFrom":[subQ1,subQ0]});Q3=makeQuery(id+"F7.imprint","IMPRINT",FACE,{"disambiguationData":[TD([[makeQuery(id+"F7.imprint","IMPRINT",EDGE,{"disambiguationData":[TD([[subQ2,-1.0]])],"derivedFrom":subQ1}),1.0]])]});}
            var Q4;
            {var subQ3=sQuery(id+"F7.wireOp",EDGE,"E65");var subQ9=sQuery(id+"F7.wireOp",EDGE,"E69.1");var subQ10=makeQuery(id+"F7.imprint","INTERSECT",VERTEX,{"disambiguationData":[OD(1.0)],"derivedFrom":[subQ3,subQ9]});Q4=makeQuery(id+"F7.imprint","IMPRINT",FACE,{"disambiguationData":[TD([[makeQuery(id+"F7.imprint","IMPRINT",EDGE,{"disambiguationData":[TD([[subQ10,-1.0]])],"derivedFrom":subQ3}),-1.0]])]});}
            var Q5;
            {var subQ0=sQuery(id+"F7.wireOp",EDGE,"E66");var subQ1=sQuery(id+"F7.wireOp",EDGE,"E51");var subQ2=makeQuery(id+"F7.imprint","INTERSECT",VERTEX,{"disambiguationData":[OD(0.0)],"derivedFrom":[subQ1,subQ0]});Q5=makeQuery(id+"F7.imprint","IMPRINT",FACE,{"disambiguationData":[TD([[makeQuery(id+"F7.imprint","IMPRINT",EDGE,{"disambiguationData":[TD([[subQ2,-1.0]])],"derivedFrom":subQ1}),-1.0]])]});}
            var Q6;
            {var subQ0=sQuery(id+"F7.wireOp",EDGE,"E66");var subQ1=makeQuery(id+"F7.imprint","IMPRINT",VERTEX,{"derivedFrom":subQ0});Q6=makeQuery(id+"F7.imprint","IMPRINT",FACE,{"disambiguationData":[TD([[makeQuery(id+"F7.imprint","IMPRINT",EDGE,{"disambiguationData":[TD([[subQ1,1.0]])],"derivedFrom":subQ0}),1.0]])]});}
            var Q7;
            {var subQ0=sQuery(id+"F7.wireOp",EDGE,"E66");var subQ1=sQuery(id+"F7.wireOp",EDGE,"E51");var subQ2=makeQuery(id+"F7.imprint","INTERSECT",VERTEX,{"disambiguationData":[OD(1.0)],"derivedFrom":[subQ1,subQ0]});Q7=makeQuery(id+"F7.imprint","IMPRINT",FACE,{"disambiguationData":[TD([[makeQuery(id+"F7.imprint","IMPRINT",EDGE,{"disambiguationData":[TD([[subQ2,-1.0]])],"derivedFrom":subQ1}),-1.0]])]});}
            var Q8;
            {var subQ6=sQuery(id+"F7.wireOp",EDGE,"Yh9rANYr-jvUk-OWzP-t44Z-ltgRU4aadTfM");Q8=makeQuery(id+"F7.imprint","IMPRINT",FACE,{"disambiguationData":[TD([[makeQuery(id+"F7.imprint","IMPRINT",EDGE,{"derivedFrom":subQ6}),-1.0]])]});}
            var Q9;
            {var subQ0=sQuery(id+"F7.wireOp",EDGE,"E74");var subQ4=sQuery(id+"F7.wireOp",EDGE,"E69.2");var subQ5=makeQuery(id+"F7.imprint","INTERSECT",VERTEX,{"disambiguationData":[OD(0.0)],"derivedFrom":[subQ4,subQ0]});Q9=makeQuery(id+"F7.imprint","IMPRINT",FACE,{"disambiguationData":[TD([[makeQuery(id+"F7.imprint","IMPRINT",EDGE,{"disambiguationData":[TD([[subQ5,-1.0]])],"derivedFrom":subQ4}),-1.0]])]});}
            var Q10;
            {var subQ0=sQuery(id+"F7.wireOp",EDGE,"E75");var subQ1=sQuery(id+"F7.wireOp",EDGE,"E69.0");var subQ2=makeQuery(id+"F7.imprint","INTERSECT",VERTEX,{"disambiguationData":[OD(0.0)],"derivedFrom":[subQ1,subQ0]});Q10=makeQuery(id+"F7.imprint","IMPRINT",FACE,{"disambiguationData":[TD([[makeQuery(id+"F7.imprint","IMPRINT",EDGE,{"disambiguationData":[TD([[subQ2,-1.0]])],"derivedFrom":subQ1}),1.0]])]});}
            var Q11;
            {var subQ0=sQuery(id+"F7.wireOp",EDGE,"E53");var subQ1=sQuery(id+"F7.wireOp",EDGE,"E52.MirrorCS");var subQ2=makeQuery(id+"F7.imprint","INTERSECT",VERTEX,{"derivedFrom":[subQ1,subQ0]});Q11=makeQuery(id+"F7.imprint","IMPRINT",FACE,{"disambiguationData":[TD([[makeQuery(id+"F7.imprint","IMPRINT",EDGE,{"disambiguationData":[TD([[subQ2,-1.0]])],"derivedFrom":subQ0}),1.0]])]});}
            var Q12;
            {var subQ0=sQuery(id+"F7.wireOp",EDGE,"E53");var subQ1=sQuery(id+"F7.wireOp",EDGE,"E51");var subQ2=makeQuery(id+"F7.imprint","INTERSECT",VERTEX,{"derivedFrom":[subQ1,subQ0]});Q12=makeQuery(id+"F7.imprint","IMPRINT",FACE,{"disambiguationData":[TD([[makeQuery(id+"F7.imprint","IMPRINT",EDGE,{"disambiguationData":[TD([[subQ2,1.0]])],"derivedFrom":subQ1}),-1.0]])]});}
            var Q13;
            {var subQ0=sQuery(id+"F7.wireOp",EDGE,"E74");var subQ1=sQuery(id+"F7.wireOp",EDGE,"E69.2");var subQ2=makeQuery(id+"F7.imprint","INTERSECT",VERTEX,{"disambiguationData":[OD(0.0)],"derivedFrom":[subQ1,subQ0]});Q13=makeQuery(id+"F7.imprint","IMPRINT",FACE,{"disambiguationData":[TD([[makeQuery(id+"F7.imprint","IMPRINT",EDGE,{"disambiguationData":[TD([[subQ2,-1.0]])],"derivedFrom":subQ1}),1.0]])]});}
            var Q14;
            {var subQ0=sQuery(id+"F7.wireOp",EDGE,"E75");var subQ1=sQuery(id+"F7.wireOp",EDGE,"E69.0");var subQ2=makeQuery(id+"F7.imprint","INTERSECT",VERTEX,{"disambiguationData":[OD(0.0)],"derivedFrom":[subQ1,subQ0]});Q14=makeQuery(id+"F7.imprint","IMPRINT",FACE,{"disambiguationData":[TD([[makeQuery(id+"F7.imprint","IMPRINT",EDGE,{"disambiguationData":[TD([[subQ2,-1.0]])],"derivedFrom":subQ1}),-1.0]])]});}
            var Q15;
            {var subQ0=sQuery(id+"F7.wireOp",EDGE,"E69.0");var subQ1=sQuery(id+"F7.wireOp",EDGE,"E66");var subQ2=makeQuery(id+"F7.imprint","INTERSECT",VERTEX,{"disambiguationData":[OD(0.0)],"derivedFrom":[subQ1,subQ0]});Q15=makeQuery(id+"F7.imprint","IMPRINT",FACE,{"disambiguationData":[TD([[makeQuery(id+"F7.imprint","IMPRINT",EDGE,{"disambiguationData":[TD([[subQ2,1.0]])],"derivedFrom":subQ1}),1.0]])]});}
            var Q16;
            {var subQ4=sQuery(id+"F7.wireOp",EDGE,"E67");Q16=makeQuery(id+"F7.imprint","IMPRINT",FACE,{"disambiguationData":[TD([[makeQuery(id+"F7.imprint","IMPRINT",EDGE,{"derivedFrom":subQ4}),1.0]])]});}
            var Q17;
            {var subQ2=sQuery(id+"F7.wireOp",EDGE,"E79");Q17=makeQuery(id+"F7.imprint","IMPRINT",FACE,{"disambiguationData":[TD([[makeQuery(id+"F7.imprint","IMPRINT",EDGE,{"derivedFrom":subQ2}),-1.0]])]});}
            var Q18;
            {var subQ0=sQuery(id+"F7.wireOp",EDGE,"E89");var subQ1=sQuery(id+"F7.wireOp",EDGE,"E69.2");var subQ2=makeQuery(id+"F7.imprint","INTERSECT",VERTEX,{"derivedFrom":[subQ1,subQ0]});Q18=makeQuery(id+"F7.imprint","IMPRINT",FACE,{"disambiguationData":[TD([[makeQuery(id+"F7.imprint","IMPRINT",EDGE,{"disambiguationData":[TD([[subQ2,1.0]])],"derivedFrom":subQ1}),1.0]])]});}
            var Q19;
            {var subQ0=sQuery(id+"F7.wireOp",EDGE,"E89");var subQ1=sQuery(id+"F7.wireOp",EDGE,"E87");var subQ2=makeQuery(id+"F7.imprint","INTERSECT",VERTEX,{"derivedFrom":[subQ1,subQ0]});Q19=makeQuery(id+"F7.imprint","IMPRINT",FACE,{"disambiguationData":[TD([[makeQuery(id+"F7.imprint","IMPRINT",EDGE,{"disambiguationData":[TD([[subQ2,-1.0]])],"derivedFrom":subQ1}),1.0]])]});}
            var Q20;
            {var subQ0=sQuery(id+"F7.wireOp",EDGE,"E88");var subQ1=sQuery(id+"F7.wireOp",EDGE,"E69.0");var subQ2=makeQuery(id+"F7.imprint","INTERSECT",VERTEX,{"derivedFrom":[subQ1,subQ0]});Q20=makeQuery(id+"F7.imprint","IMPRINT",FACE,{"disambiguationData":[TD([[makeQuery(id+"F7.imprint","IMPRINT",EDGE,{"disambiguationData":[TD([[subQ2,1.0]])],"derivedFrom":subQ1}),-1.0]])]});}
            var Q21;
            {var subQ0=sQuery(id+"F7.wireOp",EDGE,"E88");var subQ1=sQuery(id+"F7.wireOp",EDGE,"E84");var subQ2=makeQuery(id+"F7.imprint","INTERSECT",VERTEX,{"derivedFrom":[subQ1,subQ0]});Q21=makeQuery(id+"F7.imprint","IMPRINT",FACE,{"disambiguationData":[TD([[makeQuery(id+"F7.imprint","IMPRINT",EDGE,{"disambiguationData":[TD([[subQ2,1.0]])],"derivedFrom":subQ1}),1.0]])]});}
            var Q22;
            {var subQ0=sQuery(id+"F7.wireOp",EDGE,"E89");var subQ1=sQuery(id+"F7.wireOp",EDGE,"E87");var subQ2=makeQuery(id+"F7.imprint","INTERSECT",VERTEX,{"derivedFrom":[subQ1,subQ0]});Q22=makeQuery(id+"F7.imprint","IMPRINT",FACE,{"disambiguationData":[TD([[makeQuery(id+"F7.imprint","IMPRINT",EDGE,{"disambiguationData":[TD([[subQ2,1.0]])],"derivedFrom":subQ1}),1.0]])]});}
            var Q23;
            {var subQ0=sQuery(id+"F7.wireOp",EDGE,"E88");var subQ1=sQuery(id+"F7.wireOp",EDGE,"E84");var subQ2=makeQuery(id+"F7.imprint","INTERSECT",VERTEX,{"derivedFrom":[subQ1,subQ0]});Q23=makeQuery(id+"F7.imprint","IMPRINT",FACE,{"disambiguationData":[TD([[makeQuery(id+"F7.imprint","IMPRINT",EDGE,{"disambiguationData":[TD([[subQ2,-1.0]])],"derivedFrom":subQ1}),1.0]])]});}
            extrude(context, id + "F8", {"entities" : qUnion([Q0, Q1, Q2, Q3, Q4, Q5, Q6, Q7, Q8, Q9, Q10, Q11, Q12, Q13, Q14, Q15, Q16, Q17, Q18, Q19, Q20, Q21, Q22, Q23]), "depth" : 26.8 * mm});
        }
        {
            var Q0;
            Q0=makeQuery(id+"F8.opExtrude","SWEPT_FACE",FACE,{"disambiguationData":[OSD([sQuery(id+"F7.wireOp",EDGE,"E80"),sQuery(id+"F7.wireOp",EDGE,"E82")])]});
            var sketch = newSketch(context, id + "F9", { "sketchPlane" : qUnion([Q0])});
            skPoint(sketch, "E92.0", {"position": v(0, 0) * mm});
            skLineSegment(sketch, "E93.0", {"start": v(40.8, 8.5) * mm, "end": v(14, 8.5) * mm});
            skLineSegment(sketch, "E93.1", {"start": v(40.8, -71.5) * mm, "end": v(40.8, 8.5) * mm});
            skLineSegment(sketch, "E93.2", {"start": v(14, -71.5) * mm, "end": v(14, 8.5) * mm});
            skLineSegment(sketch, "E93.3", {"start": v(40.8, -71.5) * mm, "end": v(14, -71.5) * mm});
            skLineSegment(sketch, "E94", {"start": v(0, 0) * mm, "end": v(27.4, 0) * mm, "construction": true});
            skPoint(sketch, "E94.endSnap0", {"position": v(27.4, 8.5) * mm});
            skLineSegment(sketch, "E95", {"start": v(27.4, 0) * mm, "end": v(27.4, 8.5) * mm, "construction": true});
            skLineSegment(sketch, "E96", {"start": v(27.4, 0) * mm, "end": v(27.4, -71.5) * mm, "construction": true});
            skPoint(sketch, "E97", {"position": v(27.4, -31.5) * mm});
            skArc(sketch, "E98", {"start": v(50.8, -4.97) * mm, "mid": v(27.4, 3.88) * mm, "end": v(4, -4.97) * mm});
            skArc(sketch, "E99", {"start": v(50.8, -11.94) * mm, "mid": v(27.4, -1) * mm, "end": v(4, -11.94) * mm});
            skLineSegment(sketch, "E100", {"start": v(50.8, -31.5) * mm, "end": v(40.8, -31.5) * mm, "construction": true});
            skLineSegment(sketch, "E101", {"start": v(40.8, -31.5) * mm, "end": v(27.4, -31.5) * mm, "construction": true});
            skLineSegment(sketch, "E102", {"start": v(27.4, -31.5) * mm, "end": v(14, -31.5) * mm, "construction": true});
            skLineSegment(sketch, "E103", {"start": v(14, -31.5) * mm, "end": v(4, -31.5) * mm, "construction": true});
            skLineSegment(sketch, "E104", {"start": v(50.8, -4.97) * mm, "end": v(50.8, -58.03) * mm});
            skLineSegment(sketch, "E105", {"start": v(4, -4.97) * mm, "end": v(4, -58.03) * mm});
            skArc(sketch, "E106.trimOffspring", {"start": v(4, -51.06) * mm, "mid": v(27.4, -62) * mm, "end": v(50.8, -51.06) * mm});
            skArc(sketch, "E107.trimOffspring", {"start": v(4, -58.03) * mm, "mid": v(27.4, -66.88) * mm, "end": v(50.8, -58.03) * mm});
            skPoint(sketch, "E108", {"position": v(27.4, 3.88) * mm});
            skPoint(sketch, "E109", {"position": v(27.4, -66.87) * mm});
            skSolve(sketch);
        }
        {
            var Q0;
            {var subQ0=sQuery(id+"F9.wireOp",EDGE,"f21bd9bb-c9b1-4cbe-b12d-282b7d9b7768.trimOffspring");var subQ1=sQuery(id+"F9.wireOp",EDGE,"ea733c9d-159c-44b3-8fd2-d54b53117e85.0");var subQ2=makeQuery(id+"F9.imprint","INTERSECT",VERTEX,{"derivedFrom":[subQ1,subQ0]});Q0=makeQuery(id+"F9.imprint","IMPRINT",FACE,{"disambiguationData":[TD([[makeQuery(id+"F9.imprint","IMPRINT",EDGE,{"disambiguationData":[TD([[subQ2,-1.0]])],"derivedFrom":subQ1}),-1.0]])]});}
            var Q1;
            {var subQ3=sQuery(id+"F9.wireOp",EDGE,"ea733c9d-159c-44b3-8fd2-d54b53117e85.0");var subQ5=sQuery(id+"F9.wireOp",EDGE,"f21bd9bb-c9b1-4cbe-b12d-282b7d9b7768.trimOffspring");var subQ9=makeQuery(id+"F9.imprint","INTERSECT",VERTEX,{"derivedFrom":[subQ3,subQ5]});Q1=makeQuery(id+"F9.imprint","IMPRINT",FACE,{"disambiguationData":[TD([[makeQuery(id+"F9.imprint","IMPRINT",EDGE,{"disambiguationData":[TD([[subQ9,-1.0]])],"derivedFrom":subQ3}),1.0]])]});}
            var Q2;
            {var subQ0=sQuery(id+"F9.wireOp",EDGE,"f21bd9bb-c9b1-4cbe-b12d-282b7d9b7768.trimOffspring");var subQ1=sQuery(id+"F9.wireOp",EDGE,"ea733c9d-159c-44b3-8fd2-d54b53117e85.1");var subQ2=makeQuery(id+"F9.imprint","INTERSECT",VERTEX,{"derivedFrom":[subQ1,subQ0]});Q2=makeQuery(id+"F9.imprint","IMPRINT",FACE,{"disambiguationData":[TD([[makeQuery(id+"F9.imprint","IMPRINT",EDGE,{"disambiguationData":[TD([[subQ2,-1.0]])],"derivedFrom":subQ1}),1.0]])]});}
            var Q3;
            {var subQ0=sQuery(id+"F9.wireOp",EDGE,"efd01210-1cff-4bd8-b063-6b382fa81eb20.MirrorCS");var subQ1=sQuery(id+"F9.wireOp",EDGE,"ea733c9d-159c-44b3-8fd2-d54b53117e85.1");var subQ2=makeQuery(id+"F9.imprint","INTERSECT",VERTEX,{"derivedFrom":[subQ1,subQ0]});Q3=makeQuery(id+"F9.imprint","IMPRINT",FACE,{"disambiguationData":[TD([[makeQuery(id+"F9.imprint","IMPRINT",EDGE,{"disambiguationData":[TD([[subQ2,-1.0]])],"derivedFrom":subQ1}),1.0]])]});}
            var Q4;
            {var subQ5=sQuery(id+"F9.wireOp",EDGE,"ea733c9d-159c-44b3-8fd2-d54b53117e85.0");var subQ8=sQuery(id+"F9.wireOp",EDGE,"jd4rFvQn-xQ1t-mU8W-PEOJ-2sT1LIvCoojA");var subQ9=makeQuery(id+"F9.imprint","INTERSECT",VERTEX,{"derivedFrom":[subQ5,subQ8]});Q4=makeQuery(id+"F9.imprint","IMPRINT",FACE,{"disambiguationData":[TD([[makeQuery(id+"F9.imprint","IMPRINT",EDGE,{"disambiguationData":[TD([[subQ9,-1.0]])],"derivedFrom":subQ5}),1.0]])]});}
            var Q5;
            {var subQ0=sQuery(id+"F9.wireOp",EDGE,"jd4rFvQn-xQ1t-mU8W-PEOJ-2sT1LIvCoojA");var subQ1=sQuery(id+"F9.wireOp",EDGE,"ea733c9d-159c-44b3-8fd2-d54b53117e85.0");var subQ2=makeQuery(id+"F9.imprint","INTERSECT",VERTEX,{"derivedFrom":[subQ1,subQ0]});Q5=makeQuery(id+"F9.imprint","IMPRINT",FACE,{"disambiguationData":[TD([[makeQuery(id+"F9.imprint","IMPRINT",EDGE,{"disambiguationData":[TD([[subQ2,-1.0]])],"derivedFrom":subQ1}),-1.0]])]});}
            var Q6;
            {var subQ0=sQuery(id+"F9.wireOp",EDGE,"E106.trimOffspring");var subQ1=sQuery(id+"F9.wireOp",EDGE,"E93.2");var subQ2=makeQuery(id+"F9.imprint","INTERSECT",VERTEX,{"derivedFrom":[subQ1,subQ0]});Q6=makeQuery(id+"F9.imprint","IMPRINT",FACE,{"disambiguationData":[TD([[makeQuery(id+"F9.imprint","IMPRINT",EDGE,{"disambiguationData":[TD([[subQ2,-1.0]])],"derivedFrom":subQ1}),1.0]])]});}
            var Q7;
            {var subQ0=sQuery(id+"F9.wireOp",EDGE,"E106.trimOffspring");var subQ1=sQuery(id+"F9.wireOp",EDGE,"E93.1");var subQ2=makeQuery(id+"F9.imprint","INTERSECT",VERTEX,{"derivedFrom":[subQ1,subQ0]});Q7=makeQuery(id+"F9.imprint","IMPRINT",FACE,{"disambiguationData":[TD([[makeQuery(id+"F9.imprint","IMPRINT",EDGE,{"disambiguationData":[TD([[subQ2,-1.0]])],"derivedFrom":subQ1}),-1.0]])]});}
            var Q8;
            {var subQ0=sQuery(id+"F9.wireOp",EDGE,"E106.trimOffspring");var subQ1=sQuery(id+"F9.wireOp",EDGE,"E93.1");var subQ2=makeQuery(id+"F9.imprint","INTERSECT",VERTEX,{"derivedFrom":[subQ1,subQ0]});Q8=makeQuery(id+"F9.imprint","IMPRINT",FACE,{"disambiguationData":[TD([[makeQuery(id+"F9.imprint","IMPRINT",EDGE,{"disambiguationData":[TD([[subQ2,-1.0]])],"derivedFrom":subQ1}),-1.0]])]});}
            var Q9;
            {var subQ0=sQuery(id+"F9.wireOp",EDGE,"E106.trimOffspring");var subQ1=sQuery(id+"F9.wireOp",EDGE,"E93.1");var subQ2=makeQuery(id+"F9.imprint","INTERSECT",VERTEX,{"derivedFrom":[subQ1,subQ0]});Q9=makeQuery(id+"F9.imprint","IMPRINT",FACE,{"disambiguationData":[TD([[makeQuery(id+"F9.imprint","IMPRINT",EDGE,{"disambiguationData":[TD([[subQ2,-1.0]])],"derivedFrom":subQ1}),1.0]])]});}
            extrude(context, id + "F10", {"entities" : qUnion([Q0, Q1, Q2, Q3, Q4, Q5, Q6, Q7, Q8, Q9]), "depth" : 66 * mm});
        }
        {
            var Q0;
            {var subQ0=sQuery(id+"F9.wireOp",EDGE,"E98");var subQ1=sQuery(id+"F9.wireOp",EDGE,"E93.1");var subQ2=makeQuery(id+"F9.imprint","INTERSECT",VERTEX,{"derivedFrom":[subQ1,subQ0]});Q0=makeQuery(id+"F9.imprint","IMPRINT",FACE,{"disambiguationData":[TD([[makeQuery(id+"F9.imprint","IMPRINT",EDGE,{"disambiguationData":[TD([[subQ2,1.0]])],"derivedFrom":subQ1}),-1.0]])]});}
            var Q1;
            {var subQ0=sQuery(id+"F9.wireOp",EDGE,"E107.trimOffspring");var subQ1=sQuery(id+"F9.wireOp",EDGE,"E93.1");var subQ2=makeQuery(id+"F9.imprint","INTERSECT",VERTEX,{"derivedFrom":[subQ1,subQ0]});Q1=makeQuery(id+"F9.imprint","IMPRINT",FACE,{"disambiguationData":[TD([[makeQuery(id+"F9.imprint","IMPRINT",EDGE,{"disambiguationData":[TD([[subQ2,-1.0]])],"derivedFrom":subQ1}),-1.0]])]});}
            var Q2;
            {var subQ0=sQuery(id+"F9.wireOp",EDGE,"E106.trimOffspring");var subQ1=sQuery(id+"F9.wireOp",EDGE,"E93.1");var subQ2=makeQuery(id+"F9.imprint","INTERSECT",VERTEX,{"derivedFrom":[subQ1,subQ0]});Q2=makeQuery(id+"F9.imprint","IMPRINT",FACE,{"disambiguationData":[TD([[makeQuery(id+"F9.imprint","IMPRINT",EDGE,{"disambiguationData":[TD([[subQ2,-1.0]])],"derivedFrom":subQ1}),-1.0]])]});}
            var Q3;
            {var subQ0=sQuery(id+"F9.wireOp",EDGE,"E98");var subQ1=sQuery(id+"F9.wireOp",EDGE,"E93.2");var subQ2=makeQuery(id+"F9.imprint","INTERSECT",VERTEX,{"derivedFrom":[subQ1,subQ0]});Q3=makeQuery(id+"F9.imprint","IMPRINT",FACE,{"disambiguationData":[TD([[makeQuery(id+"F9.imprint","IMPRINT",EDGE,{"disambiguationData":[TD([[subQ2,1.0]])],"derivedFrom":subQ1}),1.0]])]});}
            var Q4;
            {var subQ0=sQuery(id+"F9.wireOp",EDGE,"E106.trimOffspring");var subQ1=sQuery(id+"F9.wireOp",EDGE,"E93.2");var subQ2=makeQuery(id+"F9.imprint","INTERSECT",VERTEX,{"derivedFrom":[subQ1,subQ0]});Q4=makeQuery(id+"F9.imprint","IMPRINT",FACE,{"disambiguationData":[TD([[makeQuery(id+"F9.imprint","IMPRINT",EDGE,{"disambiguationData":[TD([[subQ2,-1.0]])],"derivedFrom":subQ1}),1.0]])]});}
            var Q5;
            {var subQ0=sQuery(id+"F9.wireOp",EDGE,"E107.trimOffspring");var subQ1=sQuery(id+"F9.wireOp",EDGE,"E93.2");var subQ2=makeQuery(id+"F9.imprint","INTERSECT",VERTEX,{"derivedFrom":[subQ1,subQ0]});Q5=makeQuery(id+"F9.imprint","IMPRINT",FACE,{"disambiguationData":[TD([[makeQuery(id+"F9.imprint","IMPRINT",EDGE,{"disambiguationData":[TD([[subQ2,-1.0]])],"derivedFrom":subQ1}),1.0]])]});}
            extrude(context, id + "F11", {"entities" : qUnion([Q0, Q1, Q2, Q3, Q4, Q5]), "oppositeDirection" : true, "depth" : 9 * mm});
        }
        {
            var Q0;
            Q0=makeQuery(id+"F11.opExtrude","SWEPT_BODY",BODY,{"disambiguationData":[OSD([sQuery(id+"F9.wireOp",EDGE,"E93.2"),sQuery(id+"F9.wireOp",EDGE,"E98"),sQuery(id+"F9.wireOp",EDGE,"E105"),sQuery(id+"F9.wireOp",EDGE,"E107.trimOffspring")])]});
            var Q1;
            Q1=makeQuery(id+"F8.opExtrude","SWEPT_BODY",BODY,{"disambiguationData":[OSD([sQuery(id+"F7.wireOp",EDGE,"E51"),sQuery(id+"F7.wireOp",EDGE,"E52.MirrorCS"),sQuery(id+"F7.wireOp",EDGE,"E53"),sQuery(id+"F7.wireOp",EDGE,"E65"),sQuery(id+"F7.wireOp",EDGE,"E66"),sQuery(id+"F7.wireOp",EDGE,"E67"),sQuery(id+"F7.wireOp",EDGE,"E68.trimOffspring"),sQuery(id+"F7.wireOp",EDGE,"E69.0"),sQuery(id+"F7.wireOp",EDGE,"E69.1"),sQuery(id+"F7.wireOp",EDGE,"E69.2"),sQuery(id+"F7.wireOp",EDGE,"E74"),sQuery(id+"F7.wireOp",EDGE,"E75"),sQuery(id+"F7.wireOp",EDGE,"E77"),sQuery(id+"F7.wireOp",EDGE,"E79"),sQuery(id+"F7.wireOp",EDGE,"E80"),sQuery(id+"F7.wireOp",EDGE,"E82")])]});
            var Q2;
            Q2=makeQuery(id+"F11.opExtrude","SWEPT_BODY",BODY,{"disambiguationData":[OSD([sQuery(id+"F9.wireOp",EDGE,"E93.1"),sQuery(id+"F9.wireOp",EDGE,"E98"),sQuery(id+"F9.wireOp",EDGE,"E104"),sQuery(id+"F9.wireOp",EDGE,"E107.trimOffspring")])]});
            var Q3;
            Q3=makeQuery(id+"F10.opExtrude","SWEPT_BODY",BODY,{"disambiguationData":[OSD([sQuery(id+"F9.wireOp",EDGE,"E99"),sQuery(id+"F9.wireOp",EDGE,"E104"),sQuery(id+"F9.wireOp",EDGE,"E105"),sQuery(id+"F9.wireOp",EDGE,"E106.trimOffspring")])]});
            booleanBodies(context, id + "F12", {"operationType" : BooleanOperationType.UNION, "tools" : qUnion([Q0, Q1, Q2, Q3])});
        }
        {
            var Q0;
            Q0=makeQuery(id+"F10.opExtrude","CAP_FACE",FACE,{"disambiguationData":[OSD([sQuery(id+"F9.wireOp",EDGE,"E99"),sQuery(id+"F9.wireOp",EDGE,"E104"),sQuery(id+"F9.wireOp",EDGE,"E105"),sQuery(id+"F9.wireOp",EDGE,"E106.trimOffspring")])],"isStart":false});
            var sketch = newSketch(context, id + "F13", { "sketchPlane" : qUnion([Q0])});
            skArc(sketch, "E110.0", {"start": v(4, -51.06) * mm, "mid": v(27.4, -62) * mm, "end": v(50.8, -51.06) * mm});
            skArc(sketch, "E110.1", {"start": v(50.8, -11.94) * mm, "mid": v(27.4, -1) * mm, "end": v(4, -11.94) * mm});
            skCircle(sketch, "E111", {"center": v(27.4, -31.5) * mm, "radius": 21 * mm});
            skSolve(sketch);
        }
        {
            var Q0;
            Q0=makeQuery(id+"F13.imprint","IMPRINT",FACE,{"disambiguationData":[TD([[makeQuery(id+"F13.imprint","IMPRINT",EDGE,{"derivedFrom":sQuery(id+"F13.wireOp",EDGE,"E111")}),1.0]])]});
            extrude(context, id + "F14", {"entities" : qUnion([Q0]), "operationType" : NewBodyOperationType.ADD, "depth" : 15.4 * mm});
        }
        {
            var Q0;
            Q0=makeQuery(id+"F14.opExtrude","CAP_FACE",FACE,{"disambiguationData":[OSD([sQuery(id+"F13.wireOp",EDGE,"E111")])],"isStart":false});
            var sketch = newSketch(context, id + "F15", { "sketchPlane" : qUnion([Q0])});
            skCircle(sketch, "E112.0", {"center": v(27.4, -31.5) * mm, "radius": 21 * mm});
            skCircle(sketch, "E113", {"center": v(27.4, -31.5) * mm, "radius": 10.5 * mm});
            skCircle(sketch, "E114", {"center": v(27.4, -31.5) * mm, "radius": 4 * mm});
            skSolve(sketch);
        }
        {
            var Q0;
            Q0=makeQuery(id+"F15.imprint","IMPRINT",FACE,{"disambiguationData":[TD([[makeQuery(id+"F15.imprint","IMPRINT",EDGE,{"derivedFrom":sQuery(id+"F15.wireOp",EDGE,"E113")}),1.0]])]});
            extrude(context, id + "F16", {"entities" : qUnion([Q0]), "operationType" : NewBodyOperationType.ADD, "depth" : 3.6 * mm});
        }
        {
            var Q0;
            Q0=makeQuery(id+"F10.opExtrude","CAP_EDGE",EDGE,{"disambiguationData":[OSD([sQuery(id+"F9.wireOp",EDGE,"E99")])],"isStart":false});
            var Q1;
            Q1=makeQuery(id+"F10.opExtrude","CAP_EDGE",EDGE,{"disambiguationData":[OSD([sQuery(id+"F9.wireOp",EDGE,"E106.trimOffspring")])],"isStart":false});
            var Q2;
            Q2=makeQuery(id+"F14.opExtrude","CAP_EDGE",EDGE,{"disambiguationData":[OSD([sQuery(id+"F13.wireOp",EDGE,"E111")])],"isStart":false});
            var Q3;
            Q3=makeQuery(id+"F16.opExtrude","CAP_EDGE",EDGE,{"disambiguationData":[OSD([sQuery(id+"F15.wireOp",EDGE,"E113")])],"isStart":false});
            fillet(context, id + "F17", {"entities" : qUnion([Q0, Q1, Q2, Q3]), "radius" : 3 * mm, "tangentPropagation" : true, "allowEdgeOverflow" : false});
        }
        {
            var Q0;
            Q0=makeQuery(id+"F16.boolean.opBoolean","SPLIT",FACE,{"disambiguationData":[TD([makeQuery(id+"F16.opExtrude","SWEPT_FACE",FACE,{"disambiguationData":[OSD([sQuery(id+"F15.wireOp",EDGE,"E114")])]})])],"derivedFrom":makeQuery(id+"F14.opExtrude","CAP_FACE",FACE,{"disambiguationData":[OSD([sQuery(id+"F13.wireOp",EDGE,"E111")])],"isStart":false})});
            var Q1;
            {var subQ0=sQuery(id+"F7.wireOp",EDGE,"E69.0");Q1=makeQuery(id+"F8.opExtrude","SWEPT_FACE",FACE,{"disambiguationData":[OSD([subQ0]),TDD([makeQuery(id+"F7.imprint","IMPRINT",EDGE,{"disambiguationData":[TD([[makeQuery(id+"F7.imprint","INTERSECT",VERTEX,{"disambiguationData":[OD(1.0)],"derivedFrom":[sQuery(id+"F7.wireOp",EDGE,"E66"),subQ0]}),-1.0]])],"derivedFrom":subQ0})])]});}
            var Q2;
            Q2=makeQuery(id+"F16.opExtrude","CAP_FACE",FACE,{"disambiguationData":[OSD([sQuery(id+"F15.wireOp",EDGE,"E113"),sQuery(id+"F15.wireOp",EDGE,"E114")])],"isStart":false});
            extrude(context, id + "F18", {"entities" : qUnion([Q0]), "endBound" : BoundingType.UP_TO_SURFACE, "oppositeDirection" : true, "endBoundEntityFace" : qUnion([Q1]), "depth" : 74 * mm, "hasSecondDirection" : true, "secondDirectionBound" : SecondDirectionBoundingType.UP_TO_SURFACE, "secondDirectionOppositeDirection" : false, "secondDirectionBoundEntityFace" : qUnion([Q2]), "secondDirectionDepth" : 25 * mm});
        }
        {
            var Q0;
            Q0=makeQuery(id+"F11.opExtrude","SWEPT_BODY",BODY,{"disambiguationData":[OSD([sQuery(id+"F9.wireOp",EDGE,"E93.2"),sQuery(id+"F9.wireOp",EDGE,"E98"),sQuery(id+"F9.wireOp",EDGE,"E105"),sQuery(id+"F9.wireOp",EDGE,"E107.trimOffspring")])]});
            var Q1;
            Q1=makeQuery(id+"F5.opExtrude","SWEPT_BODY",BODY,{"disambiguationData":[OSD([sQuery(id+"F2.wireOp",EDGE,"E12"),sQuery(id+"F2.wireOp",EDGE,"E13.3"),sQuery(id+"F2.wireOp",EDGE,"E13.4"),sQuery(id+"F2.wireOp",EDGE,"E20"),sQuery(id+"F2.wireOp",EDGE,"E22"),sQuery(id+"F2.wireOp",EDGE,"E23"),sQuery(id+"F2.wireOp",EDGE,"E24"),sQuery(id+"F2.wireOp",EDGE,"E25")])]});
            booleanBodies(context, id + "F19", {"operationType" : BooleanOperationType.SUBTRACTION, "tools" : qUnion([Q0]), "targets" : qUnion([Q1]), "keepTools" : true});
        }
        {
            var Q0;
            {var subQ0=sQuery(id+"F3.wireOp",EDGE,"E29.3");Q0=makeQuery(id+"F3.imprint","IMPRINT",FACE,{"disambiguationData":[TD([[makeQuery(id+"F3.imprint","IMPRINT",EDGE,{"derivedFrom":subQ0}),1.0]])]});}
            var sketch = newSketch(context, id + "F20", { "sketchPlane" : qUnion([Q0])});
            skPoint(sketch, "E115.0", {"position": v(0, 0) * mm});
            skLineSegment(sketch, "E115.1", {"start": v(-43.9, -78) * mm, "end": v(40.1, -78) * mm});
            skLineSegment(sketch, "E115.2", {"start": v(-32.9, -76) * mm, "end": v(32.9, -76) * mm});
            skLineSegment(sketch, "E115.3", {"start": v(40.1, -76) * mm, "end": v(40.1, -8) * mm});
            skLineSegment(sketch, "E115.4", {"start": v(38.1, -76) * mm, "end": v(38.1, 33) * mm});
            skLineSegment(sketch, "E115.5", {"start": v(-41.9, 33) * mm, "end": v(-41.9, -76) * mm});
            skLineSegment(sketch, "E115.6", {"start": v(-43.9, -35) * mm, "end": v(-43.9, -76) * mm});
            skLineSegment(sketch, "E115.7", {"start": v(0, 35) * mm, "end": v(-55.25, 35) * mm});
            skLineSegment(sketch, "E115.8", {"start": v(55.25, 35) * mm, "end": v(0, 35) * mm});
            skLineSegment(sketch, "E115.9", {"start": v(53.25, 33) * mm, "end": v(0, 33) * mm});
            skLineSegment(sketch, "E115.10", {"start": v(0, 33) * mm, "end": v(-53.25, 33) * mm});
            skLineSegment(sketch, "E115.11", {"start": v(-43.9, -35) * mm, "end": v(-43.9, -8) * mm});
            skLineSegment(sketch, "E115.12", {"start": v(-41.9, -76) * mm, "end": v(-32.9, -76) * mm});
            skLineSegment(sketch, "E115.13", {"start": v(38.1, -76) * mm, "end": v(32.9, -76) * mm});
            skLineSegment(sketch, "E115.14", {"start": v(40.1, -78) * mm, "end": v(40.1, -76) * mm});
            skLineSegment(sketch, "E115.15", {"start": v(38.1, -76) * mm, "end": v(40.1, -76) * mm});
            skLineSegment(sketch, "E115.16", {"start": v(-43.9, -76) * mm, "end": v(-43.9, -78) * mm});
            skLineSegment(sketch, "E115.17", {"start": v(-43.9, -76) * mm, "end": v(-41.9, -76) * mm});
            skLineSegment(sketch, "E116", {"start": v(-43.9, -8) * mm, "end": v(-43.9, 33) * mm});
            skLineSegment(sketch, "E117", {"start": v(40.1, -8) * mm, "end": v(40.1, 33) * mm});
            skLineSegment(sketch, "E118", {"start": v(40.1, 33) * mm, "end": v(40.1, 35) * mm});
            skLineSegment(sketch, "E119", {"start": v(-43.9, 33) * mm, "end": v(-43.9, 35) * mm});
            skLineSegment(sketch, "E120", {"start": v(-31.9, 33) * mm, "end": v(-31.9, 31) * mm});
            skLineSegment(sketch, "E121", {"start": v(-31.9, 31) * mm, "end": v(-41.9, 31) * mm});
            skLineSegment(sketch, "E122", {"start": v(-32.9, -76) * mm, "end": v(-32.9, -74) * mm});
            skLineSegment(sketch, "E123", {"start": v(-32.9, -74) * mm, "end": v(-41.9, -74) * mm});
            skLineSegment(sketch, "E124", {"start": v(0, 33) * mm, "end": v(0, -76) * mm, "construction": true});
            skPoint(sketch, "E125", {"position": v(0, -66) * mm});
            skPoint(sketch, "E126", {"position": v(0, -46) * mm});
            skSolve(sketch);
        }
        {
            var Q0;
            {var subQ2=sQuery(id+"F20.wireOp",EDGE,"E118");Q0=makeQuery(id+"F20.imprint","IMPRINT",FACE,{"disambiguationData":[TD([[makeQuery(id+"F20.imprint","IMPRINT",EDGE,{"derivedFrom":subQ2}),1.0]])]});}
            var Q1;
            {var subQ0=sQuery(id+"F20.wireOp",EDGE,"E115.9");var subQ1=sQuery(id+"F20.wireOp",EDGE,"E115.4");var subQ2=makeQuery(id+"F20.imprint","INTERSECT",VERTEX,{"derivedFrom":[subQ1,subQ0]});Q1=makeQuery(id+"F20.imprint","IMPRINT",FACE,{"disambiguationData":[TD([[makeQuery(id+"F20.imprint","IMPRINT",EDGE,{"disambiguationData":[TD([[subQ2,1.0]])],"derivedFrom":subQ0}),1.0]])]});}
            var Q2;
            {var subQ1=sQuery(id+"F20.wireOp",EDGE,"E115.3");Q2=makeQuery(id+"F20.imprint","IMPRINT",FACE,{"disambiguationData":[TD([[makeQuery(id+"F20.imprint","IMPRINT",EDGE,{"derivedFrom":subQ1}),1.0]])]});}
            var Q3;
            Q3=makeQuery(id+"F20.imprint","IMPRINT",FACE,{"disambiguationData":[TD([[makeQuery(id+"F20.imprint","IMPRINT",EDGE,{"derivedFrom":sQuery(id+"F20.wireOp",EDGE,"E115.1")}),1.0]])]});
            extrude(context, id + "F21", {"entities" : qUnion([Q0, Q1, Q2, Q3]), "depth" : 125 * mm});
        }
        {
            var Q0;
            {var subQ1=sQuery(id+"F20.wireOp",EDGE,"E115.5");Q0=makeQuery(id+"F20.imprint","IMPRINT",FACE,{"disambiguationData":[TD([[makeQuery(id+"F20.imprint","IMPRINT",EDGE,{"derivedFrom":subQ1}),-1.0]])]});}
            var Q1;
            {var subQ4=sQuery(id+"F20.wireOp",EDGE,"E120");Q1=makeQuery(id+"F20.imprint","IMPRINT",FACE,{"disambiguationData":[TD([[makeQuery(id+"F20.imprint","IMPRINT",EDGE,{"derivedFrom":subQ4}),-1.0]])]});}
            var Q2;
            {var subQ0=sQuery(id+"F20.wireOp",EDGE,"E115.12");Q2=makeQuery(id+"F20.imprint","IMPRINT",FACE,{"disambiguationData":[TD([[makeQuery(id+"F20.imprint","IMPRINT",EDGE,{"derivedFrom":subQ0}),1.0]])]});}
            extrude(context, id + "F22", {"entities" : qUnion([Q0, Q1, Q2]), "depth" : 123 * mm});
        }
        {
            var Q0;
            Q0=makeQuery(id+"F11.opExtrude","SWEPT_BODY",BODY,{"disambiguationData":[OSD([sQuery(id+"F9.wireOp",EDGE,"E93.2"),sQuery(id+"F9.wireOp",EDGE,"E98"),sQuery(id+"F9.wireOp",EDGE,"E105"),sQuery(id+"F9.wireOp",EDGE,"E107.trimOffspring")])]});
            var Q1;
            Q1=makeQuery(id+"F22.opExtrude","SWEPT_BODY",BODY,{"disambiguationData":[OSD([sQuery(id+"F20.wireOp",EDGE,"E115.5"),sQuery(id+"F20.wireOp",EDGE,"E115.6"),sQuery(id+"F20.wireOp",EDGE,"E115.10"),sQuery(id+"F20.wireOp",EDGE,"E115.11"),sQuery(id+"F20.wireOp",EDGE,"E115.12"),sQuery(id+"F20.wireOp",EDGE,"E115.17"),sQuery(id+"F20.wireOp",EDGE,"E116"),sQuery(id+"F20.wireOp",EDGE,"E120"),sQuery(id+"F20.wireOp",EDGE,"E121"),sQuery(id+"F20.wireOp",EDGE,"E122"),sQuery(id+"F20.wireOp",EDGE,"E123")])]});
            booleanBodies(context, id + "F23", {"operationType" : BooleanOperationType.SUBTRACTION, "tools" : qUnion([Q0]), "targets" : qUnion([Q1]), "keepTools" : true});
        }
        {
            var Q0;
            Q0=makeQuery(id+"F22.opExtrude","SWEPT_FACE",FACE,{"disambiguationData":[OSD([sQuery(id+"F20.wireOp",EDGE,"E115.5")])]});
            var sketch = newSketch(context, id + "F24", { "sketchPlane" : qUnion([Q0])});
            skLineSegment(sketch, "E127.0", {"start": v(-127, 31) * mm, "end": v(-4, 31) * mm});
            skLineSegment(sketch, "E127.1", {"start": v(-127, -76) * mm, "end": v(-127, 29) * mm});
            skLineSegment(sketch, "E127.2", {"start": v(-127, -74) * mm, "end": v(-4, -74) * mm});
            skLineSegment(sketch, "E127.3", {"start": v(-50.8, -51.06) * mm, "end": v(-50.8, -11.94) * mm});
            skLineSegment(sketch, "E128", {"start": v(-61, 29) * mm, "end": v(-50.8, 29) * mm});
            skLineSegment(sketch, "E129", {"start": v(-61, -46) * mm, "end": v(-126, -46) * mm});
            skLineSegment(sketch, "E130", {"start": v(-126, -46) * mm, "end": v(-126, 29) * mm});
            skLineSegment(sketch, "E131", {"start": v(-61, -46) * mm, "end": v(-61, 29) * mm});
            skLineSegment(sketch, "E132", {"start": v(-61, 29) * mm, "end": v(-126, 29) * mm});
            skLineSegment(sketch, "E133", {"start": v(-126, 29) * mm, "end": v(-127, 29) * mm});
            skLineSegment(sketch, "E134.trimOffspring", {"start": v(-127, 31) * mm, "end": v(-127, 33) * mm});
            skLineSegment(sketch, "E135", {"start": v(-127, 29) * mm, "end": v(-127, 31) * mm});
            skSolve(sketch);
        }
        {
            var Q0;
            Q0=makeQuery(id+"F24.imprint","IMPRINT",FACE,{"disambiguationData":[TD([[makeQuery(id+"F24.imprint","IMPRINT",EDGE,{"derivedFrom":sQuery(id+"F24.wireOp",EDGE,"E129")}),-1.0]])]});
            extrude(context, id + "F25", {"entities" : qUnion([Q0]), "depth" : 40 * mm});
        }
        {
            var Q0;
            Q0=makeQuery(id+"F18.opExtrude","SWEPT_BODY",BODY,{"disambiguationData":[OSD([sQuery(id+"F13.wireOp",EDGE,"E111")])]});
            var Q1;
            Q1=makeQuery(id+"F11.opExtrude","SWEPT_BODY",BODY,{"disambiguationData":[OSD([sQuery(id+"F9.wireOp",EDGE,"E93.2"),sQuery(id+"F9.wireOp",EDGE,"E98"),sQuery(id+"F9.wireOp",EDGE,"E105"),sQuery(id+"F9.wireOp",EDGE,"E107.trimOffspring")])]});
            booleanBodies(context, id + "F26", {"operationType" : BooleanOperationType.SUBTRACTION, "tools" : qUnion([Q0]), "targets" : qUnion([Q1]), "keepTools" : true});
        }
        {
            var Q0;
            Q0=qCreatedBy(makeId("Front.planeOp"),FACE);
            var sketch = newSketch(context, id + "F27", { "sketchPlane" : qUnion([Q0])});
            skLineSegment(sketch, "E136.5", {"start": v(-41.9, 33) * mm, "end": v(-41.9, -4.97) * mm});
            skLineSegment(sketch, "E136.6", {"start": v(38.1, 33) * mm, "end": v(-41.9, 33) * mm});
            skLineSegment(sketch, "E137.0", {"start": v(55.25, 35) * mm, "end": v(-55.25, 35) * mm});
            skLineSegment(sketch, "E137.1", {"start": v(-55.25, 35) * mm, "end": v(-55.25, -8) * mm});
            skCircle(sketch, "E137.2", {"center": v(-45, 17.5) * mm, "radius": 3.3 * mm});
            skArc(sketch, "E138.0", {"start": v(24.54, 21.92) * mm, "mid": v(-7.62, 32) * mm, "end": v(-31.78, 8.5) * mm});
            skLineSegment(sketch, "E139", {"start": v(-33.87, 2.96) * mm, "end": v(-33.87, 33) * mm, "construction": true});
            skPoint(sketch, "E140", {"position": v(-33.87, 19.5) * mm});
            skPoint(sketch, "E141.0", {"position": v(-33.87, 2.96) * mm});
            skPoint(sketch, "E141.1", {"position": v(28.32, -20.57) * mm});
            skPoint(sketch, "E141.2", {"position": v(28.32, -69.57) * mm});
            skPoint(sketch, "E141.3", {"position": v(-27.68, -69.57) * mm});
            skPoint(sketch, "E141.4", {"position": v(27.85, 19.5) * mm});
            skPoint(sketch, "E142.0", {"position": v(-41.9, 33) * mm});
            skPoint(sketch, "E143.0", {"position": v(-41.9, -4.97) * mm});
            skLineSegment(sketch, "E144.0", {"start": v(-41.9, 33) * mm, "end": v(-41.9, 23.5) * mm});
            skLineSegment(sketch, "E144.1", {"start": v(-41.9, 11.5) * mm, "end": v(-41.9, -4.97) * mm});
            skSolve(sketch);
        }
        {
            var Q0;
            Q0=sQuery(id+"F27.wireOp",VERTEX,"E140");
            var Q1;
            Q1=makeQuery(id+"F4.opExtrude","SWEPT_BODY",BODY,{"disambiguationData":[OSD([sQuery(id+"F3.wireOp",EDGE,"E29.5"),sQuery(id+"F3.wireOp",EDGE,"E29.6"),sQuery(id+"F3.wireOp",EDGE,"E29.7"),sQuery(id+"F3.wireOp",EDGE,"E29.8"),sQuery(id+"F3.wireOp",EDGE,"E29.9"),sQuery(id+"F3.wireOp",EDGE,"E31"),sQuery(id+"F3.wireOp",EDGE,"E32"),sQuery(id+"F3.wireOp",EDGE,"E36.0"),sQuery(id+"F3.wireOp",EDGE,"E38"),sQuery(id+"F3.wireOp",EDGE,"E40"),sQuery(id+"F3.wireOp",EDGE,"E41"),sQuery(id+"F3.wireOp",EDGE,"E42"),sQuery(id+"F3.wireOp",EDGE,"E43")])]});
            var Q2;
            Q2=makeQuery(id+"F5.opExtrude","SWEPT_BODY",BODY,{"disambiguationData":[OSD([sQuery(id+"F2.wireOp",EDGE,"E12"),sQuery(id+"F2.wireOp",EDGE,"E13.3"),sQuery(id+"F2.wireOp",EDGE,"E13.4"),sQuery(id+"F2.wireOp",EDGE,"E20"),sQuery(id+"F2.wireOp",EDGE,"E22"),sQuery(id+"F2.wireOp",EDGE,"E23"),sQuery(id+"F2.wireOp",EDGE,"E24"),sQuery(id+"F2.wireOp",EDGE,"E25"),sQuery(id+"F2.wireOp",EDGE,"E26")])]});
            hole(context, id + "F28", {"style" : HoleStyle.C_SINK, "endStyle" : HoleEndStyle.THROUGH, "oppositeDirection" : true, "standardTappedOrClearance" : lookupTablePath({ "standard" : "ISO", "fit" : "Normal", "size" : "M5", "type" : "Clearance" }), "standardBlindInLast" : lookupTablePath({ "fit" : "Standard", "standard" : "ISO", "size" : "M5", "type" : "Clearance" }), "holeDiameter" : 5.5 * mm, "cSinkDiameter" : 11.2 * mm, "cSinkAngle" : 90 * degree, "startFromSketch" : true, "locations" : qUnion([Q0]), "scope" : qUnion([Q1, Q2]), "isTappedThrough" : true});
        }
        {
            var Q0;
            Q0=sQuery(id+"F27.wireOp",VERTEX,"E141.4");
            var Q1;
            Q1=sQuery(id+"F27.wireOp",VERTEX,"E141.1");
            var Q2;
            Q2=sQuery(id+"F27.wireOp",VERTEX,"E141.2");
            var Q3;
            Q3=sQuery(id+"F27.wireOp",VERTEX,"E141.3");
            var Q4;
            Q4=sQuery(id+"F27.wireOp",VERTEX,"E141.0");
            var Q5;
            Q5=makeQuery(id+"F4.opExtrude","SWEPT_BODY",BODY,{"disambiguationData":[OSD([sQuery(id+"F3.wireOp",EDGE,"E29.5"),sQuery(id+"F3.wireOp",EDGE,"E29.6"),sQuery(id+"F3.wireOp",EDGE,"E29.7"),sQuery(id+"F3.wireOp",EDGE,"E29.8"),sQuery(id+"F3.wireOp",EDGE,"E29.9"),sQuery(id+"F3.wireOp",EDGE,"E31"),sQuery(id+"F3.wireOp",EDGE,"E32"),sQuery(id+"F3.wireOp",EDGE,"E36.0"),sQuery(id+"F3.wireOp",EDGE,"E38"),sQuery(id+"F3.wireOp",EDGE,"E40"),sQuery(id+"F3.wireOp",EDGE,"E41"),sQuery(id+"F3.wireOp",EDGE,"E42"),sQuery(id+"F3.wireOp",EDGE,"E43")])]});
            var Q6;
            Q6=makeQuery(id+"F5.opExtrude","SWEPT_BODY",BODY,{"disambiguationData":[OSD([sQuery(id+"F2.wireOp",EDGE,"E12"),sQuery(id+"F2.wireOp",EDGE,"E13.3"),sQuery(id+"F2.wireOp",EDGE,"E13.4"),sQuery(id+"F2.wireOp",EDGE,"E20"),sQuery(id+"F2.wireOp",EDGE,"E22"),sQuery(id+"F2.wireOp",EDGE,"E23"),sQuery(id+"F2.wireOp",EDGE,"E24"),sQuery(id+"F2.wireOp",EDGE,"E25")])]});
            var Q7;
            Q7=makeQuery(id+"F11.opExtrude","SWEPT_BODY",BODY,{"disambiguationData":[OSD([sQuery(id+"F9.wireOp",EDGE,"E93.2"),sQuery(id+"F9.wireOp",EDGE,"E98"),sQuery(id+"F9.wireOp",EDGE,"E105"),sQuery(id+"F9.wireOp",EDGE,"E107.trimOffspring")])]});
            hole(context, id + "F29", {"style" : HoleStyle.C_SINK, "endStyle" : HoleEndStyle.THROUGH, "oppositeDirection" : true, "standardTappedOrClearance" : lookupTablePath({ "standard" : "ISO", "fit" : "Close", "size" : "M5", "type" : "Clearance" }), "standardBlindInLast" : lookupTablePath({ "fit" : "Close", "standard" : "ISO", "size" : "M5", "type" : "Clearance" }), "holeDiameter" : 5.25 * mm, "cSinkDiameter" : 11.2 * mm, "cSinkAngle" : 90 * degree, "startFromSketch" : true, "locations" : qUnion([Q0, Q1, Q2, Q3, Q4]), "scope" : qUnion([Q5, Q6, Q7]), "isTappedThrough" : true});
        }
        {
            var Q0;
            {var subQ0=sQuery(id+"F7.wireOp",EDGE,"E69.0");Q0=makeQuery(id+"F8.opExtrude","SWEPT_FACE",FACE,{"disambiguationData":[OSD([subQ0]),TDD([makeQuery(id+"F7.imprint","IMPRINT",EDGE,{"disambiguationData":[TD([[makeQuery(id+"F7.imprint","INTERSECT",VERTEX,{"derivedFrom":[subQ0,sQuery(id+"F7.wireOp",EDGE,"E91")]}),1.0]])],"derivedFrom":subQ0})])]});}
            var sketch = newSketch(context, id + "F30", { "sketchPlane" : qUnion([Q0])});
            skCircle(sketch, "E145.0", {"center": v(27.4, -31.5) * mm, "radius": 4 * mm});
            skLineSegment(sketch, "E145.1", {"start": v(40.8, -24.78) * mm, "end": v(40.8, -32.1) * mm});
            skLineSegment(sketch, "E145.2", {"start": v(14, -24.78) * mm, "end": v(14, -32.1) * mm});
            skLineSegment(sketch, "E145.3", {"start": v(40.8, -32.1) * mm, "end": v(14, -32.1) * mm});
            skCircle(sketch, "E146", {"center": v(27.4, -31.5) * mm, "radius": 6.6 * mm});
            skSolve(sketch);
        }
        {
            var Q0;
            Q0=makeQuery(id+"F30.imprint","IMPRINT",FACE,{"disambiguationData":[TD([[makeQuery(id+"F30.imprint","IMPRINT",EDGE,{"derivedFrom":sQuery(id+"F30.wireOp",EDGE,"E145.0")}),-1.0]])]});
            extrude(context, id + "F31", {"entities" : qUnion([Q0]), "operationType" : NewBodyOperationType.ADD, "depth" : 13.2 * mm});
        }
        {
            var Q0;
            {var subQ0=sQuery(id+"F7.wireOp",EDGE,"E69.2");Q0=makeQuery(id+"F8.opExtrude","SWEPT_FACE",FACE,{"disambiguationData":[OSD([subQ0]),TDD([makeQuery(id+"F7.imprint","IMPRINT",EDGE,{"disambiguationData":[TD([[makeQuery(id+"F7.imprint","INTERSECT",VERTEX,{"derivedFrom":[sQuery(id+"F7.wireOp",EDGE,"E69.1"),subQ0]}),-1.0]])],"derivedFrom":subQ0})])]});}
            var sketch = newSketch(context, id + "F32", { "sketchPlane" : qUnion([Q0])});
            skCircle(sketch, "E147.0", {"center": v(-27.4, -31.5) * mm, "radius": 4 * mm});
            skLineSegment(sketch, "E147.1", {"start": v(-14, 0) * mm, "end": v(-14, -76.1) * mm});
            skLineSegment(sketch, "E147.2", {"start": v(-40.8, 0) * mm, "end": v(-40.8, -34.1) * mm});
            skLineSegment(sketch, "E147.3", {"start": v(-40.8, 0) * mm, "end": v(-14, 0) * mm});
            skLineSegment(sketch, "E148", {"start": v(-27.4, -31.5) * mm, "end": v(-27.4, -20.5) * mm, "construction": true});
            skLineSegment(sketch, "E149", {"start": v(-40.8, -20.5) * mm, "end": v(-14, -20.5) * mm});
            skLineSegment(sketch, "E150", {"start": v(-40.8, -42.5) * mm, "end": v(-14, -42.5) * mm});
            skLineSegment(sketch, "E151", {"start": v(-40.8, -42.5) * mm, "end": v(-40.8, -34.1) * mm});
            skSolve(sketch);
        }
        {
            var Q0;
            Q0=makeQuery(id+"F32.imprint","IMPRINT",FACE,{"disambiguationData":[TD([[makeQuery(id+"F32.imprint","IMPRINT",EDGE,{"derivedFrom":sQuery(id+"F32.wireOp",EDGE,"E147.0")}),-1.0]])]});
            extrude(context, id + "F33", {"entities" : qUnion([Q0]), "operationType" : NewBodyOperationType.ADD, "depth" : 7 * mm});
        }
        {
            var Q0;
            Q0=makeQuery(id+"F22.opExtrude","SWEPT_BODY",BODY,{"disambiguationData":[OSD([sQuery(id+"F20.wireOp",EDGE,"E115.5"),sQuery(id+"F20.wireOp",EDGE,"E115.6"),sQuery(id+"F20.wireOp",EDGE,"E115.10"),sQuery(id+"F20.wireOp",EDGE,"E115.11"),sQuery(id+"F20.wireOp",EDGE,"E115.12"),sQuery(id+"F20.wireOp",EDGE,"E115.17"),sQuery(id+"F20.wireOp",EDGE,"E116"),sQuery(id+"F20.wireOp",EDGE,"E120"),sQuery(id+"F20.wireOp",EDGE,"E121"),sQuery(id+"F20.wireOp",EDGE,"E122"),sQuery(id+"F20.wireOp",EDGE,"E123")])]});
            var Q1;
            Q1=makeQuery(id+"F5.opExtrude","SWEPT_BODY",BODY,{"disambiguationData":[OSD([sQuery(id+"F2.wireOp",EDGE,"E12"),sQuery(id+"F2.wireOp",EDGE,"E13.3"),sQuery(id+"F2.wireOp",EDGE,"E13.4"),sQuery(id+"F2.wireOp",EDGE,"E20"),sQuery(id+"F2.wireOp",EDGE,"E22"),sQuery(id+"F2.wireOp",EDGE,"E23"),sQuery(id+"F2.wireOp",EDGE,"E24"),sQuery(id+"F2.wireOp",EDGE,"E25")])]});
            booleanBodies(context, id + "F34", {"operationType" : BooleanOperationType.SUBTRACTION, "tools" : qUnion([Q0]), "targets" : qUnion([Q1]), "keepTools" : true});
        }
        {
            var Q0;
            Q0=sQuery(id+"F20.wireOp",VERTEX,"E126");
            var Q1;
            Q1=sQuery(id+"F20.wireOp",VERTEX,"E125");
            var Q2;
            Q2=makeQuery(id+"F5.opExtrude","SWEPT_BODY",BODY,{"disambiguationData":[OSD([sQuery(id+"F2.wireOp",EDGE,"E12"),sQuery(id+"F2.wireOp",EDGE,"E13.3"),sQuery(id+"F2.wireOp",EDGE,"E13.4"),sQuery(id+"F2.wireOp",EDGE,"E20"),sQuery(id+"F2.wireOp",EDGE,"E22"),sQuery(id+"F2.wireOp",EDGE,"E23"),sQuery(id+"F2.wireOp",EDGE,"E24"),sQuery(id+"F2.wireOp",EDGE,"E25")])]});
            hole(context, id + "F35", {"style" : HoleStyle.C_BORE, "endStyle" : HoleEndStyle.THROUGH, "oppositeDirection" : true, "standardTappedOrClearance" : lookupTablePath({ "standard" : "ISO", "fit" : "Normal", "size" : "M5", "type" : "Clearance" }), "standardBlindInLast" : lookupTablePath({ "fit" : "Standard", "standard" : "ISO", "size" : "M5", "type" : "Clearance" }), "holeDiameter" : 5.5 * mm, "cBoreDiameter" : 9.75 * mm, "cBoreDepth" : 5 * mm, "startFromSketch" : true, "locations" : qUnion([Q0, Q1]), "scope" : qUnion([Q2]), "isTappedThrough" : true});
        }
        {
            var Q0;
            Q0=makeQuery(id+"F21.opExtrude","SWEPT_FACE",FACE,{"disambiguationData":[OSD([sQuery(id+"F20.wireOp",EDGE,"E115.3"),sQuery(id+"F20.wireOp",EDGE,"E115.14"),sQuery(id+"F20.wireOp",EDGE,"E117"),sQuery(id+"F20.wireOp",EDGE,"E118")])]});
            var sketch = newSketch(context, id + "F36", { "sketchPlane" : qUnion([Q0])});
            skLineSegment(sketch, "E152.0", {"start": v(-129, 35) * mm, "end": v(-4, 35) * mm});
            skLineSegment(sketch, "E152.1", {"start": v(-129, -78) * mm, "end": v(-129, 35) * mm});
            skLineSegment(sketch, "E152.2", {"start": v(-129, -78) * mm, "end": v(-4, -78) * mm});
            skLineSegment(sketch, "E152.3", {"start": v(-4, -76) * mm, "end": v(-4, 33) * mm});
            skPoint(sketch, "E153.0", {"position": v(0, 0) * mm});
            skLineSegment(sketch, "E154", {"start": v(0, 0) * mm, "end": v(-48, 0) * mm, "construction": true});
            skLineSegment(sketch, "E155", {"start": v(-48, -78) * mm, "end": v(-48, 0) * mm, "construction": true});
            skPoint(sketch, "E156", {"position": v(-48, -45) * mm});
            skSolve(sketch);
        }
        {
            var Q0;
            Q0=sQuery(id+"F36.wireOp",VERTEX,"E156");
            var Q1;
            Q1=makeQuery(id+"F21.opExtrude","SWEPT_BODY",BODY,{"disambiguationData":[OSD([sQuery(id+"F20.wireOp",EDGE,"E115.1"),sQuery(id+"F20.wireOp",EDGE,"E115.2"),sQuery(id+"F20.wireOp",EDGE,"E115.3"),sQuery(id+"F20.wireOp",EDGE,"E115.4"),sQuery(id+"F20.wireOp",EDGE,"E115.7"),sQuery(id+"F20.wireOp",EDGE,"E115.8"),sQuery(id+"F20.wireOp",EDGE,"E115.9"),sQuery(id+"F20.wireOp",EDGE,"E115.10"),sQuery(id+"F20.wireOp",EDGE,"E115.12"),sQuery(id+"F20.wireOp",EDGE,"E115.13"),sQuery(id+"F20.wireOp",EDGE,"E115.14"),sQuery(id+"F20.wireOp",EDGE,"E115.16"),sQuery(id+"F20.wireOp",EDGE,"E115.17"),sQuery(id+"F20.wireOp",EDGE,"E117"),sQuery(id+"F20.wireOp",EDGE,"E118"),sQuery(id+"F20.wireOp",EDGE,"E119")])]});
            hole(context, id + "F37", {"style" : HoleStyle.SIMPLE, "endStyle" : HoleEndStyle.THROUGH, "standardTappedOrClearance" : lookupTablePath({ "standard" : "ISO", "size" : "8.1", "type" : "Drilled" }), "standardBlindInLast" : lookupTablePath({ "standard" : "ISO", "size" : "8.1", "type" : "Drilled" }), "holeDiameter" : 8.1 * mm, "startFromSketch" : true, "locations" : qUnion([Q0]), "scope" : qUnion([Q1]), "isTappedThrough" : true});
        }
    });
